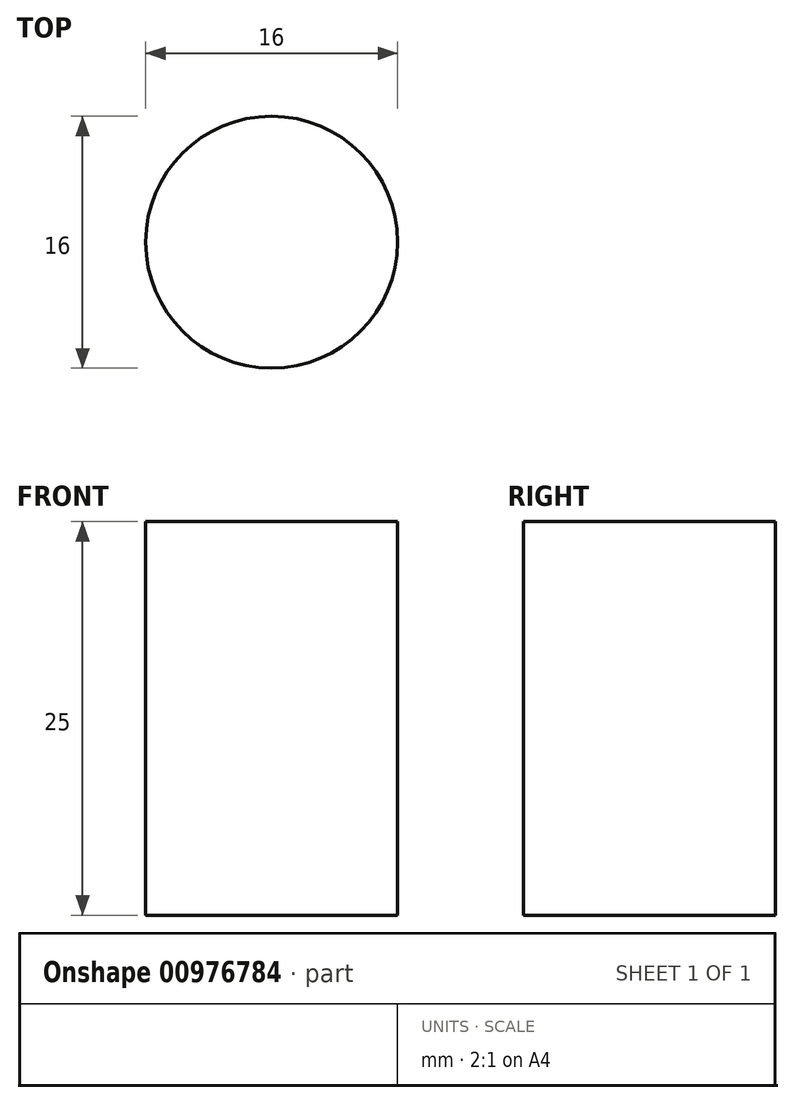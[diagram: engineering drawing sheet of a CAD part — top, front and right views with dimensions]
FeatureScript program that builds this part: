
annotation { "Feature Type Name" : "Feature", "Feature Type Description" : "" }
export const myFeature = defineFeature(function(context is Context, id is Id, definition is map)
    precondition{}
    {
        {
            var Q0;
            Q0=qCreatedBy(makeId("Top.planeOp"),FACE);
            var sketch = newSketch(context, id + "F0", { "sketchPlane" : qUnion([Q0])});
            skCircle(sketch, "E0", {"center": v(-27.11, 19.72) * mm, "radius": 8 * mm});
            skCircle(sketch, "E1", {"center": v(-10.34, 31.9) * mm, "radius": 8 * mm});
            skCircle(sketch, "E2", {"center": v(10.38, 31.88) * mm, "radius": 8 * mm});
            skCircle(sketch, "E3", {"center": v(27.13, 19.69) * mm, "radius": 8 * mm});
            skCircle(sketch, "E4", {"center": v(33.52, -0.02) * mm, "radius": 8 * mm});
            skCircle(sketch, "E5", {"center": v(27.11, -19.72) * mm, "radius": 8 * mm});
            skCircle(sketch, "E6", {"center": v(10.34, -31.9) * mm, "radius": 8 * mm});
            skCircle(sketch, "E7", {"center": v(-10.38, -31.88) * mm, "radius": 8 * mm});
            skCircle(sketch, "E8", {"center": v(-27.13, -19.69) * mm, "radius": 8 * mm});
            skCircle(sketch, "E9", {"center": v(-33.52, 0.02) * mm, "radius": 8 * mm});
            skCircle(sketch, "E10", {"center": v(0, 0) * mm, "radius": 11 * mm});
            skArc(sketch, "E11", {"start": v(4.75, 47.29) * mm, "mid": v(4.67, 47.25) * mm, "end": v(4.61, 47.18) * mm});
            skArc(sketch, "E12", {"start": v(4.61, 47.18) * mm, "mid": v(4.58, 47.11) * mm, "end": v(4.55, 47.04) * mm});
            skArc(sketch, "E13", {"start": v(3.36, 47.14) * mm, "mid": v(3.91, 46.61) * mm, "end": v(4.55, 47.04) * mm});
            skArc(sketch, "E14", {"start": v(3.36, 47.14) * mm, "mid": v(3.34, 47.22) * mm, "end": v(3.32, 47.3) * mm});
            skArc(sketch, "E15", {"start": v(3.32, 47.3) * mm, "mid": v(3.27, 47.37) * mm, "end": v(3.2, 47.42) * mm});
            skArc(sketch, "E16", {"start": v(5.18, 47.24) * mm, "mid": v(4.97, 47.26) * mm, "end": v(4.75, 47.29) * mm});
            skArc(sketch, "E17", {"start": v(6.73, 47.05) * mm, "mid": v(6.65, 47.01) * mm, "end": v(6.59, 46.95) * mm});
            skArc(sketch, "E18", {"start": v(6.59, 46.95) * mm, "mid": v(6.55, 46.88) * mm, "end": v(6.52, 46.81) * mm});
            skArc(sketch, "E19", {"start": v(5.33, 46.96) * mm, "mid": v(5.86, 46.4) * mm, "end": v(6.52, 46.81) * mm});
            skArc(sketch, "E20", {"start": v(5.33, 46.96) * mm, "mid": v(5.32, 47.04) * mm, "end": v(5.3, 47.1) * mm});
            skArc(sketch, "E21", {"start": v(5.3, 47.1) * mm, "mid": v(5.25, 47.19) * mm, "end": v(5.18, 47.24) * mm});
            skArc(sketch, "E22", {"start": v(7.16, 46.98) * mm, "mid": v(6.94, 47.02) * mm, "end": v(6.73, 47.05) * mm});
            skArc(sketch, "E23", {"start": v(8.7, 46.72) * mm, "mid": v(8.61, 46.7) * mm, "end": v(8.55, 46.63) * mm});
            skArc(sketch, "E24", {"start": v(8.55, 46.63) * mm, "mid": v(8.5, 46.57) * mm, "end": v(8.47, 46.5) * mm});
            skArc(sketch, "E25", {"start": v(7.29, 46.7) * mm, "mid": v(7.8, 46.12) * mm, "end": v(8.47, 46.5) * mm});
            skArc(sketch, "E26", {"start": v(7.29, 46.7) * mm, "mid": v(7.28, 46.77) * mm, "end": v(7.26, 46.85) * mm});
            skArc(sketch, "E27", {"start": v(7.26, 46.85) * mm, "mid": v(7.22, 46.93) * mm, "end": v(7.16, 46.98) * mm});
            skArc(sketch, "E28", {"start": v(9.12, 46.64) * mm, "mid": v(8.9, 46.68) * mm, "end": v(8.7, 46.72) * mm});
            skArc(sketch, "E29", {"start": v(10.64, 46.32) * mm, "mid": v(10.56, 46.29) * mm, "end": v(10.5, 46.23) * mm});
            skArc(sketch, "E30", {"start": v(10.5, 46.23) * mm, "mid": v(10.45, 46.17) * mm, "end": v(10.41, 46.1) * mm});
            skArc(sketch, "E31", {"start": v(9.24, 46.35) * mm, "mid": v(9.73, 45.75) * mm, "end": v(10.41, 46.1) * mm});
            skArc(sketch, "E32", {"start": v(9.24, 46.35) * mm, "mid": v(9.23, 46.43) * mm, "end": v(9.22, 46.5) * mm});
            skArc(sketch, "E33", {"start": v(9.22, 46.5) * mm, "mid": v(9.18, 46.58) * mm, "end": v(9.12, 46.64) * mm});
            skArc(sketch, "E34", {"start": v(11.06, 46.22) * mm, "mid": v(10.85, 46.27) * mm, "end": v(10.64, 46.32) * mm});
            skArc(sketch, "E35", {"start": v(12.57, 45.83) * mm, "mid": v(12.49, 45.8) * mm, "end": v(12.42, 45.75) * mm});
            skArc(sketch, "E36", {"start": v(12.42, 45.75) * mm, "mid": v(12.37, 45.7) * mm, "end": v(12.33, 45.62) * mm});
            skArc(sketch, "E37", {"start": v(11.17, 45.92) * mm, "mid": v(11.63, 45.3) * mm, "end": v(12.33, 45.62) * mm});
            skArc(sketch, "E38", {"start": v(11.17, 45.92) * mm, "mid": v(11.17, 46) * mm, "end": v(11.16, 46.07) * mm});
            skArc(sketch, "E39", {"start": v(11.16, 46.07) * mm, "mid": v(11.12, 46.16) * mm, "end": v(11.06, 46.22) * mm});
            skArc(sketch, "E40", {"start": v(12.99, 45.72) * mm, "mid": v(12.78, 45.77) * mm, "end": v(12.57, 45.83) * mm});
            skArc(sketch, "E41", {"start": v(14.48, 45.27) * mm, "mid": v(14.4, 45.24) * mm, "end": v(14.32, 45.2) * mm});
            skArc(sketch, "E42", {"start": v(14.32, 45.2) * mm, "mid": v(14.27, 45.13) * mm, "end": v(14.23, 45.07) * mm});
            skArc(sketch, "E43", {"start": v(13.08, 45.41) * mm, "mid": v(13.52, 44.78) * mm, "end": v(14.23, 45.07) * mm});
            skArc(sketch, "E44", {"start": v(13.08, 45.41) * mm, "mid": v(13.09, 45.5) * mm, "end": v(13.08, 45.57) * mm});
            skArc(sketch, "E45", {"start": v(13.08, 45.57) * mm, "mid": v(13.05, 45.65) * mm, "end": v(12.99, 45.72) * mm});
            skArc(sketch, "E46", {"start": v(14.9, 45.13) * mm, "mid": v(14.69, 45.2) * mm, "end": v(14.48, 45.27) * mm});
            skArc(sketch, "E47", {"start": v(16.36, 44.62) * mm, "mid": v(16.28, 44.6) * mm, "end": v(16.2, 44.55) * mm});
            skArc(sketch, "E48", {"start": v(16.2, 44.55) * mm, "mid": v(16.15, 44.5) * mm, "end": v(16.1, 44.43) * mm});
            skArc(sketch, "E49", {"start": v(14.97, 44.83) * mm, "mid": v(15.38, 44.17) * mm, "end": v(16.1, 44.43) * mm});
            skArc(sketch, "E50", {"start": v(14.97, 44.83) * mm, "mid": v(14.98, 44.9) * mm, "end": v(14.97, 44.98) * mm});
            skArc(sketch, "E51", {"start": v(14.97, 44.98) * mm, "mid": v(14.95, 45.06) * mm, "end": v(14.9, 45.13) * mm});
            skArc(sketch, "E52", {"start": v(16.77, 44.47) * mm, "mid": v(16.57, 44.54) * mm, "end": v(16.36, 44.62) * mm});
            skArc(sketch, "E53", {"start": v(18.22, 43.9) * mm, "mid": v(18.13, 43.88) * mm, "end": v(18.05, 43.83) * mm});
            skArc(sketch, "E54", {"start": v(18.05, 43.83) * mm, "mid": v(18, 43.78) * mm, "end": v(17.96, 43.72) * mm});
            skArc(sketch, "E55", {"start": v(16.84, 44.16) * mm, "mid": v(17.22, 43.5) * mm, "end": v(17.96, 43.72) * mm});
            skArc(sketch, "E56", {"start": v(16.84, 44.16) * mm, "mid": v(16.85, 44.24) * mm, "end": v(16.85, 44.31) * mm});
            skArc(sketch, "E57", {"start": v(16.85, 44.31) * mm, "mid": v(16.82, 44.4) * mm, "end": v(16.77, 44.47) * mm});
            skArc(sketch, "E58", {"start": v(18.62, 43.73) * mm, "mid": v(18.42, 43.81) * mm, "end": v(18.22, 43.9) * mm});
            skArc(sketch, "E59", {"start": v(20.04, 43.1) * mm, "mid": v(19.95, 43.08) * mm, "end": v(19.87, 43.04) * mm});
            skArc(sketch, "E60", {"start": v(19.87, 43.04) * mm, "mid": v(19.82, 42.99) * mm, "end": v(19.77, 42.93) * mm});
            skArc(sketch, "E61", {"start": v(18.67, 43.42) * mm, "mid": v(19.03, 42.73) * mm, "end": v(19.77, 42.93) * mm});
            skArc(sketch, "E62", {"start": v(18.67, 43.42) * mm, "mid": v(18.68, 43.5) * mm, "end": v(18.69, 43.57) * mm});
            skArc(sketch, "E63", {"start": v(18.69, 43.57) * mm, "mid": v(18.67, 43.65) * mm, "end": v(18.62, 43.73) * mm});
            skArc(sketch, "E64", {"start": v(20.43, 42.9) * mm, "mid": v(20.24, 43) * mm, "end": v(20.04, 43.1) * mm});
            skArc(sketch, "E65", {"start": v(21.83, 42.22) * mm, "mid": v(21.74, 42.2) * mm, "end": v(21.66, 42.17) * mm});
            skArc(sketch, "E66", {"start": v(21.66, 42.17) * mm, "mid": v(21.6, 42.12) * mm, "end": v(21.55, 42.06) * mm});
            skArc(sketch, "E67", {"start": v(20.47, 42.6) * mm, "mid": v(20.8, 41.9) * mm, "end": v(21.55, 42.06) * mm});
            skArc(sketch, "E68", {"start": v(20.47, 42.6) * mm, "mid": v(20.49, 42.67) * mm, "end": v(20.5, 42.75) * mm});
            skArc(sketch, "E69", {"start": v(20.5, 42.75) * mm, "mid": v(20.48, 42.83) * mm, "end": v(20.43, 42.9) * mm});
            skArc(sketch, "E70", {"start": v(22.2, 42.02) * mm, "mid": v(22.02, 42.12) * mm, "end": v(21.83, 42.22) * mm});
            skArc(sketch, "E71", {"start": v(23.58, 41.27) * mm, "mid": v(23.49, 41.26) * mm, "end": v(23.4, 41.23) * mm});
            skArc(sketch, "E72", {"start": v(23.4, 41.23) * mm, "mid": v(23.35, 41.18) * mm, "end": v(23.3, 41.12) * mm});
            skArc(sketch, "E73", {"start": v(22.24, 41.7) * mm, "mid": v(22.53, 40.99) * mm, "end": v(23.3, 41.12) * mm});
            skArc(sketch, "E74", {"start": v(22.24, 41.7) * mm, "mid": v(22.26, 41.78) * mm, "end": v(22.27, 41.85) * mm});
            skArc(sketch, "E75", {"start": v(22.27, 41.85) * mm, "mid": v(22.25, 41.94) * mm, "end": v(22.2, 42.02) * mm});
            skArc(sketch, "E76", {"start": v(23.95, 41.05) * mm, "mid": v(23.76, 41.16) * mm, "end": v(23.58, 41.27) * mm});
            skArc(sketch, "E77", {"start": v(25.28, 40.24) * mm, "mid": v(25.2, 40.24) * mm, "end": v(25.11, 40.2) * mm});
            skArc(sketch, "E78", {"start": v(25.11, 40.2) * mm, "mid": v(25.05, 40.16) * mm, "end": v(25, 40.11) * mm});
            skArc(sketch, "E79", {"start": v(23.97, 40.73) * mm, "mid": v(24.23, 40.01) * mm, "end": v(25, 40.11) * mm});
            skArc(sketch, "E80", {"start": v(23.97, 40.73) * mm, "mid": v(23.99, 40.8) * mm, "end": v(24, 40.88) * mm});
            skArc(sketch, "E81", {"start": v(24, 40.88) * mm, "mid": v(24, 40.97) * mm, "end": v(23.95, 41.05) * mm});
            skArc(sketch, "E82", {"start": v(25.65, 40.01) * mm, "mid": v(25.47, 40.13) * mm, "end": v(25.28, 40.24) * mm});
            skArc(sketch, "E83", {"start": v(26.95, 39.15) * mm, "mid": v(26.86, 39.15) * mm, "end": v(26.77, 39.12) * mm});
            skArc(sketch, "E84", {"start": v(26.77, 39.12) * mm, "mid": v(26.71, 39.08) * mm, "end": v(26.65, 39.03) * mm});
            skArc(sketch, "E85", {"start": v(25.65, 39.7) * mm, "mid": v(25.89, 38.96) * mm, "end": v(26.65, 39.03) * mm});
            skArc(sketch, "E86", {"start": v(25.65, 39.7) * mm, "mid": v(25.68, 39.77) * mm, "end": v(25.7, 39.84) * mm});
            skArc(sketch, "E87", {"start": v(25.7, 39.84) * mm, "mid": v(25.69, 39.93) * mm, "end": v(25.65, 40.01) * mm});
            skArc(sketch, "E88", {"start": v(27.3, 38.9) * mm, "mid": v(27.12, 39.03) * mm, "end": v(26.95, 39.15) * mm});
            skArc(sketch, "E89", {"start": v(28.56, 37.99) * mm, "mid": v(28.47, 38) * mm, "end": v(28.39, 37.97) * mm});
            skArc(sketch, "E90", {"start": v(28.39, 37.97) * mm, "mid": v(28.32, 37.93) * mm, "end": v(28.26, 37.88) * mm});
            skArc(sketch, "E91", {"start": v(27.3, 38.59) * mm, "mid": v(27.5, 37.84) * mm, "end": v(28.26, 37.88) * mm});
            skArc(sketch, "E92", {"start": v(27.3, 38.59) * mm, "mid": v(27.32, 38.66) * mm, "end": v(27.34, 38.73) * mm});
            skArc(sketch, "E93", {"start": v(27.34, 38.73) * mm, "mid": v(27.33, 38.82) * mm, "end": v(27.3, 38.9) * mm});
            skArc(sketch, "E94", {"start": v(28.9, 37.72) * mm, "mid": v(28.73, 37.86) * mm, "end": v(28.56, 37.99) * mm});
            skArc(sketch, "E95", {"start": v(30.13, 36.76) * mm, "mid": v(30.04, 36.77) * mm, "end": v(29.95, 36.74) * mm});
            skArc(sketch, "E96", {"start": v(29.95, 36.74) * mm, "mid": v(29.89, 36.7) * mm, "end": v(29.82, 36.66) * mm});
            skArc(sketch, "E97", {"start": v(28.88, 37.4) * mm, "mid": v(29.05, 36.66) * mm, "end": v(29.82, 36.66) * mm});
            skArc(sketch, "E98", {"start": v(28.88, 37.4) * mm, "mid": v(28.91, 37.48) * mm, "end": v(28.93, 37.55) * mm});
            skArc(sketch, "E99", {"start": v(28.93, 37.55) * mm, "mid": v(28.94, 37.64) * mm, "end": v(28.9, 37.72) * mm});
            skArc(sketch, "E100", {"start": v(30.46, 36.48) * mm, "mid": v(30.3, 36.62) * mm, "end": v(30.13, 36.76) * mm});
            skArc(sketch, "E101", {"start": v(31.64, 35.46) * mm, "mid": v(31.55, 35.48) * mm, "end": v(31.47, 35.46) * mm});
            skArc(sketch, "E102", {"start": v(31.47, 35.46) * mm, "mid": v(31.4, 35.42) * mm, "end": v(31.33, 35.38) * mm});
            skArc(sketch, "E103", {"start": v(30.43, 36.17) * mm, "mid": v(30.56, 35.4) * mm, "end": v(31.33, 35.38) * mm});
            skArc(sketch, "E104", {"start": v(30.43, 36.17) * mm, "mid": v(30.46, 36.24) * mm, "end": v(30.48, 36.3) * mm});
            skArc(sketch, "E105", {"start": v(30.48, 36.3) * mm, "mid": v(30.49, 36.4) * mm, "end": v(30.46, 36.48) * mm});
            skArc(sketch, "E106", {"start": v(31.96, 35.17) * mm, "mid": v(31.8, 35.32) * mm, "end": v(31.64, 35.46) * mm});
            skArc(sketch, "E107", {"start": v(33.1, 34.1) * mm, "mid": v(33.01, 34.12) * mm, "end": v(32.92, 34.1) * mm});
            skArc(sketch, "E108", {"start": v(32.92, 34.1) * mm, "mid": v(32.85, 34.08) * mm, "end": v(32.79, 34.04) * mm});
            skArc(sketch, "E109", {"start": v(31.91, 34.86) * mm, "mid": v(32.02, 34.1) * mm, "end": v(32.79, 34.04) * mm});
            skArc(sketch, "E110", {"start": v(31.91, 34.86) * mm, "mid": v(31.95, 34.93) * mm, "end": v(31.98, 35) * mm});
            skArc(sketch, "E111", {"start": v(31.98, 35) * mm, "mid": v(31.98, 35.09) * mm, "end": v(31.96, 35.17) * mm});
            skArc(sketch, "E112", {"start": v(33.4, 33.8) * mm, "mid": v(33.25, 33.96) * mm, "end": v(33.1, 34.1) * mm});
            skArc(sketch, "E113", {"start": v(34.5, 32.7) * mm, "mid": v(34.41, 32.71) * mm, "end": v(34.32, 32.7) * mm});
            skArc(sketch, "E114", {"start": v(34.32, 32.7) * mm, "mid": v(34.25, 32.67) * mm, "end": v(34.18, 32.64) * mm});
            skArc(sketch, "E115", {"start": v(33.34, 33.5) * mm, "mid": v(33.42, 32.73) * mm, "end": v(34.18, 32.64) * mm});
            skArc(sketch, "E116", {"start": v(33.34, 33.5) * mm, "mid": v(33.38, 33.56) * mm, "end": v(33.41, 33.63) * mm});
            skArc(sketch, "E117", {"start": v(33.41, 33.63) * mm, "mid": v(33.43, 33.72) * mm, "end": v(33.4, 33.8) * mm});
            skArc(sketch, "E118", {"start": v(34.8, 32.38) * mm, "mid": v(34.64, 32.53) * mm, "end": v(34.5, 32.7) * mm});
            skArc(sketch, "E119", {"start": v(35.83, 31.22) * mm, "mid": v(35.75, 31.24) * mm, "end": v(35.66, 31.24) * mm});
            skArc(sketch, "E120", {"start": v(35.66, 31.24) * mm, "mid": v(35.59, 31.2) * mm, "end": v(35.52, 31.18) * mm});
            skArc(sketch, "E121", {"start": v(34.72, 32.07) * mm, "mid": v(34.76, 31.3) * mm, "end": v(35.52, 31.18) * mm});
            skArc(sketch, "E122", {"start": v(34.72, 32.07) * mm, "mid": v(34.76, 32.13) * mm, "end": v(34.8, 32.2) * mm});
            skArc(sketch, "E123", {"start": v(34.8, 32.2) * mm, "mid": v(34.8, 32.29) * mm, "end": v(34.8, 32.38) * mm});
            skArc(sketch, "E124", {"start": v(36.12, 30.89) * mm, "mid": v(35.98, 31.05) * mm, "end": v(35.83, 31.22) * mm});
            skArc(sketch, "E125", {"start": v(37.11, 29.69) * mm, "mid": v(37.03, 29.72) * mm, "end": v(36.94, 29.71) * mm});
            skArc(sketch, "E126", {"start": v(36.94, 29.71) * mm, "mid": v(36.87, 29.7) * mm, "end": v(36.8, 29.66) * mm});
            skArc(sketch, "E127", {"start": v(36.03, 30.59) * mm, "mid": v(36.04, 29.82) * mm, "end": v(36.8, 29.66) * mm});
            skArc(sketch, "E128", {"start": v(36.03, 30.59) * mm, "mid": v(36.07, 30.65) * mm, "end": v(36.1, 30.72) * mm});
            skArc(sketch, "E129", {"start": v(36.1, 30.72) * mm, "mid": v(36.13, 30.8) * mm, "end": v(36.12, 30.89) * mm});
            skArc(sketch, "E130", {"start": v(37.38, 29.35) * mm, "mid": v(37.25, 29.52) * mm, "end": v(37.11, 29.69) * mm});
            skArc(sketch, "E131", {"start": v(38.32, 28.1) * mm, "mid": v(38.24, 28.14) * mm, "end": v(38.15, 28.14) * mm});
            skArc(sketch, "E132", {"start": v(38.15, 28.14) * mm, "mid": v(38.08, 28.12) * mm, "end": v(38, 28.1) * mm});
            skArc(sketch, "E133", {"start": v(37.28, 29.05) * mm, "mid": v(37.26, 28.28) * mm, "end": v(38, 28.1) * mm});
            skArc(sketch, "E134", {"start": v(37.28, 29.05) * mm, "mid": v(37.33, 29.11) * mm, "end": v(37.36, 29.18) * mm});
            skArc(sketch, "E135", {"start": v(37.36, 29.18) * mm, "mid": v(37.39, 29.26) * mm, "end": v(37.38, 29.35) * mm});
            skArc(sketch, "E136", {"start": v(38.58, 27.76) * mm, "mid": v(38.45, 27.93) * mm, "end": v(38.32, 28.1) * mm});
            skArc(sketch, "E137", {"start": v(39.46, 26.48) * mm, "mid": v(39.38, 26.52) * mm, "end": v(39.3, 26.52) * mm});
            skArc(sketch, "E138", {"start": v(39.3, 26.52) * mm, "mid": v(39.22, 26.5) * mm, "end": v(39.15, 26.48) * mm});
            skArc(sketch, "E139", {"start": v(38.46, 27.46) * mm, "mid": v(38.4, 26.7) * mm, "end": v(39.15, 26.48) * mm});
            skArc(sketch, "E140", {"start": v(38.46, 27.46) * mm, "mid": v(38.51, 27.52) * mm, "end": v(38.55, 27.59) * mm});
            skArc(sketch, "E141", {"start": v(38.55, 27.59) * mm, "mid": v(38.58, 27.67) * mm, "end": v(38.58, 27.76) * mm});
            skArc(sketch, "E142", {"start": v(39.7, 26.12) * mm, "mid": v(39.58, 26.3) * mm, "end": v(39.46, 26.48) * mm});
            skArc(sketch, "E143", {"start": v(40.54, 24.8) * mm, "mid": v(40.46, 24.84) * mm, "end": v(40.37, 24.85) * mm});
            skArc(sketch, "E144", {"start": v(40.37, 24.85) * mm, "mid": v(40.3, 24.84) * mm, "end": v(40.22, 24.82) * mm});
            skArc(sketch, "E145", {"start": v(39.58, 25.83) * mm, "mid": v(39.5, 25.06) * mm, "end": v(40.22, 24.82) * mm});
            skArc(sketch, "E146", {"start": v(39.58, 25.83) * mm, "mid": v(39.63, 25.89) * mm, "end": v(39.67, 25.95) * mm});
            skArc(sketch, "E147", {"start": v(39.67, 25.95) * mm, "mid": v(39.7, 26.03) * mm, "end": v(39.7, 26.12) * mm});
            skArc(sketch, "E148", {"start": v(40.76, 24.43) * mm, "mid": v(40.65, 24.62) * mm, "end": v(40.54, 24.8) * mm});
            skArc(sketch, "E149", {"start": v(41.54, 23.08) * mm, "mid": v(41.46, 23.13) * mm, "end": v(41.38, 23.14) * mm});
            skArc(sketch, "E150", {"start": v(41.38, 23.14) * mm, "mid": v(41.3, 23.13) * mm, "end": v(41.23, 23.1) * mm});
            skArc(sketch, "E151", {"start": v(40.63, 24.15) * mm, "mid": v(40.5, 23.39) * mm, "end": v(41.23, 23.1) * mm});
            skArc(sketch, "E152", {"start": v(40.63, 24.15) * mm, "mid": v(40.68, 24.2) * mm, "end": v(40.73, 24.26) * mm});
            skArc(sketch, "E153", {"start": v(40.73, 24.26) * mm, "mid": v(40.76, 24.35) * mm, "end": v(40.76, 24.43) * mm});
            skArc(sketch, "E154", {"start": v(41.75, 22.7) * mm, "mid": v(41.65, 22.9) * mm, "end": v(41.54, 23.08) * mm});
            skArc(sketch, "E155", {"start": v(42.47, 21.32) * mm, "mid": v(42.4, 21.37) * mm, "end": v(42.3, 21.38) * mm});
            skArc(sketch, "E156", {"start": v(42.3, 21.38) * mm, "mid": v(42.23, 21.38) * mm, "end": v(42.16, 21.36) * mm});
            skArc(sketch, "E157", {"start": v(41.6, 22.43) * mm, "mid": v(41.45, 21.67) * mm, "end": v(42.16, 21.36) * mm});
            skArc(sketch, "E158", {"start": v(41.6, 22.43) * mm, "mid": v(41.66, 22.48) * mm, "end": v(41.7, 22.54) * mm});
            skArc(sketch, "E159", {"start": v(41.7, 22.54) * mm, "mid": v(41.74, 22.62) * mm, "end": v(41.75, 22.7) * mm});
            skArc(sketch, "E160", {"start": v(42.66, 20.94) * mm, "mid": v(42.57, 21.13) * mm, "end": v(42.47, 21.32) * mm});
            skArc(sketch, "E161", {"start": v(43.33, 19.53) * mm, "mid": v(43.25, 19.58) * mm, "end": v(43.17, 19.6) * mm});
            skArc(sketch, "E162", {"start": v(43.17, 19.6) * mm, "mid": v(43.1, 19.6) * mm, "end": v(43.02, 19.58) * mm});
            skArc(sketch, "E163", {"start": v(42.5, 20.66) * mm, "mid": v(42.32, 19.92) * mm, "end": v(43.02, 19.58) * mm});
            skArc(sketch, "E164", {"start": v(42.5, 20.66) * mm, "mid": v(42.56, 20.71) * mm, "end": v(42.61, 20.77) * mm});
            skArc(sketch, "E165", {"start": v(42.61, 20.77) * mm, "mid": v(42.66, 20.85) * mm, "end": v(42.66, 20.94) * mm});
            skArc(sketch, "E166", {"start": v(43.5, 19.13) * mm, "mid": v(43.42, 19.33) * mm, "end": v(43.33, 19.53) * mm});
            skArc(sketch, "E167", {"start": v(44.1, 17.7) * mm, "mid": v(44.04, 17.75) * mm, "end": v(43.95, 17.77) * mm});
            skArc(sketch, "E168", {"start": v(43.95, 17.77) * mm, "mid": v(43.87, 17.77) * mm, "end": v(43.8, 17.76) * mm});
            skArc(sketch, "E169", {"start": v(43.33, 18.87) * mm, "mid": v(43.12, 18.13) * mm, "end": v(43.8, 17.76) * mm});
            skArc(sketch, "E170", {"start": v(43.33, 18.87) * mm, "mid": v(43.4, 18.91) * mm, "end": v(43.45, 18.97) * mm});
            skArc(sketch, "E171", {"start": v(43.45, 18.97) * mm, "mid": v(43.5, 19.04) * mm, "end": v(43.5, 19.13) * mm});
            skArc(sketch, "E172", {"start": v(44.27, 17.3) * mm, "mid": v(44.19, 17.5) * mm, "end": v(44.1, 17.7) * mm});
            skArc(sketch, "E173", {"start": v(44.8, 15.83) * mm, "mid": v(44.74, 15.89) * mm, "end": v(44.66, 15.91) * mm});
            skArc(sketch, "E174", {"start": v(44.66, 15.91) * mm, "mid": v(44.58, 15.92) * mm, "end": v(44.5, 15.91) * mm});
            skArc(sketch, "E175", {"start": v(44.09, 17.04) * mm, "mid": v(43.84, 16.3) * mm, "end": v(44.5, 15.91) * mm});
            skArc(sketch, "E176", {"start": v(44.09, 17.04) * mm, "mid": v(44.15, 17.08) * mm, "end": v(44.2, 17.13) * mm});
            skArc(sketch, "E177", {"start": v(44.2, 17.13) * mm, "mid": v(44.25, 17.2) * mm, "end": v(44.27, 17.3) * mm});
            skArc(sketch, "E178", {"start": v(44.95, 15.43) * mm, "mid": v(44.88, 15.63) * mm, "end": v(44.8, 15.83) * mm});
            skArc(sketch, "E179", {"start": v(45.43, 13.94) * mm, "mid": v(45.37, 14) * mm, "end": v(45.28, 14.03) * mm});
            skArc(sketch, "E180", {"start": v(45.28, 14.03) * mm, "mid": v(45.2, 14.04) * mm, "end": v(45.13, 14.03) * mm});
            skArc(sketch, "E181", {"start": v(44.76, 15.17) * mm, "mid": v(44.49, 14.45) * mm, "end": v(45.13, 14.03) * mm});
            skArc(sketch, "E182", {"start": v(44.76, 15.17) * mm, "mid": v(44.82, 15.22) * mm, "end": v(44.88, 15.27) * mm});
            skArc(sketch, "E183", {"start": v(44.88, 15.27) * mm, "mid": v(44.93, 15.34) * mm, "end": v(44.95, 15.43) * mm});
            skArc(sketch, "E184", {"start": v(45.56, 13.53) * mm, "mid": v(45.5, 13.74) * mm, "end": v(45.43, 13.94) * mm});
            skArc(sketch, "E185", {"start": v(45.98, 12.03) * mm, "mid": v(45.91, 12.09) * mm, "end": v(45.83, 12.12) * mm});
            skArc(sketch, "E186", {"start": v(45.83, 12.12) * mm, "mid": v(45.76, 12.13) * mm, "end": v(45.68, 12.13) * mm});
            skArc(sketch, "E187", {"start": v(45.36, 13.29) * mm, "mid": v(45.05, 12.58) * mm, "end": v(45.68, 12.13) * mm});
            skArc(sketch, "E188", {"start": v(45.36, 13.29) * mm, "mid": v(45.42, 13.33) * mm, "end": v(45.48, 13.37) * mm});
            skArc(sketch, "E189", {"start": v(45.48, 13.37) * mm, "mid": v(45.54, 13.44) * mm, "end": v(45.56, 13.53) * mm});
            skArc(sketch, "E190", {"start": v(46.09, 11.6) * mm, "mid": v(46.03, 11.82) * mm, "end": v(45.98, 12.03) * mm});
            skArc(sketch, "E191", {"start": v(46.44, 10.1) * mm, "mid": v(46.38, 10.16) * mm, "end": v(46.3, 10.2) * mm});
            skArc(sketch, "E192", {"start": v(46.3, 10.2) * mm, "mid": v(46.22, 10.2) * mm, "end": v(46.15, 10.2) * mm});
            skArc(sketch, "E193", {"start": v(45.87, 11.38) * mm, "mid": v(45.54, 10.68) * mm, "end": v(46.15, 10.2) * mm});
            skArc(sketch, "E194", {"start": v(45.87, 11.38) * mm, "mid": v(45.94, 11.41) * mm, "end": v(46, 11.46) * mm});
            skArc(sketch, "E195", {"start": v(46, 11.46) * mm, "mid": v(46.06, 11.53) * mm, "end": v(46.09, 11.6) * mm});
            skArc(sketch, "E196", {"start": v(46.53, 9.67) * mm, "mid": v(46.49, 9.88) * mm, "end": v(46.44, 10.1) * mm});
            skArc(sketch, "E197", {"start": v(46.82, 8.14) * mm, "mid": v(46.76, 8.2) * mm, "end": v(46.68, 8.24) * mm});
            skArc(sketch, "E198", {"start": v(46.68, 8.24) * mm, "mid": v(46.6, 8.26) * mm, "end": v(46.53, 8.27) * mm});
            skArc(sketch, "E199", {"start": v(46.3, 9.45) * mm, "mid": v(45.95, 8.76) * mm, "end": v(46.53, 8.27) * mm});
            skArc(sketch, "E200", {"start": v(46.3, 9.45) * mm, "mid": v(46.38, 9.48) * mm, "end": v(46.44, 9.52) * mm});
            skArc(sketch, "E201", {"start": v(46.44, 9.52) * mm, "mid": v(46.5, 9.59) * mm, "end": v(46.53, 9.67) * mm});
            skArc(sketch, "E202", {"start": v(46.9, 7.71) * mm, "mid": v(46.86, 7.93) * mm, "end": v(46.82, 8.14) * mm});
            skArc(sketch, "E203", {"start": v(47.12, 6.17) * mm, "mid": v(47.07, 6.24) * mm, "end": v(46.99, 6.28) * mm});
            skArc(sketch, "E204", {"start": v(46.99, 6.28) * mm, "mid": v(46.91, 6.3) * mm, "end": v(46.84, 6.3) * mm});
            skArc(sketch, "E205", {"start": v(46.66, 7.5) * mm, "mid": v(46.27, 6.83) * mm, "end": v(46.84, 6.3) * mm});
            skArc(sketch, "E206", {"start": v(46.66, 7.5) * mm, "mid": v(46.73, 7.53) * mm, "end": v(46.8, 7.57) * mm});
            skArc(sketch, "E207", {"start": v(46.8, 7.57) * mm, "mid": v(46.86, 7.63) * mm, "end": v(46.9, 7.71) * mm});
            skArc(sketch, "E208", {"start": v(47.18, 5.74) * mm, "mid": v(47.15, 5.96) * mm, "end": v(47.12, 6.17) * mm});
            skArc(sketch, "E209", {"start": v(47.34, 4.2) * mm, "mid": v(47.29, 4.26) * mm, "end": v(47.21, 4.3) * mm});
            skArc(sketch, "E210", {"start": v(47.21, 4.3) * mm, "mid": v(47.14, 4.33) * mm, "end": v(47.06, 4.34) * mm});
            skArc(sketch, "E211", {"start": v(46.94, 5.54) * mm, "mid": v(46.52, 4.89) * mm, "end": v(47.06, 4.34) * mm});
            skArc(sketch, "E212", {"start": v(46.94, 5.54) * mm, "mid": v(47, 5.57) * mm, "end": v(47.07, 5.6) * mm});
            skArc(sketch, "E213", {"start": v(47.07, 5.6) * mm, "mid": v(47.14, 5.66) * mm, "end": v(47.18, 5.74) * mm});
            skArc(sketch, "E214", {"start": v(47.38, 3.76) * mm, "mid": v(47.36, 3.98) * mm, "end": v(47.34, 4.2) * mm});
            skArc(sketch, "E215", {"start": v(47.47, 2.2) * mm, "mid": v(47.42, 2.28) * mm, "end": v(47.35, 2.33) * mm});
            skArc(sketch, "E216", {"start": v(47.35, 2.33) * mm, "mid": v(47.28, 2.35) * mm, "end": v(47.2, 2.37) * mm});
            skArc(sketch, "E217", {"start": v(47.13, 3.57) * mm, "mid": v(46.68, 2.94) * mm, "end": v(47.2, 2.37) * mm});
            skArc(sketch, "E218", {"start": v(47.13, 3.57) * mm, "mid": v(47.2, 3.6) * mm, "end": v(47.27, 3.63) * mm});
            skArc(sketch, "E219", {"start": v(47.27, 3.63) * mm, "mid": v(47.34, 3.68) * mm, "end": v(47.38, 3.76) * mm});
            skArc(sketch, "E220", {"start": v(47.5, 1.77) * mm, "mid": v(47.48, 2) * mm, "end": v(47.47, 2.2) * mm});
            skArc(sketch, "E221", {"start": v(47.52, 0.22) * mm, "mid": v(47.48, 0.3) * mm, "end": v(47.4, 0.34) * mm});
            skArc(sketch, "E222", {"start": v(47.4, 0.34) * mm, "mid": v(47.33, 0.37) * mm, "end": v(47.26, 0.39) * mm});
            skArc(sketch, "E223", {"start": v(47.24, 1.59) * mm, "mid": v(46.77, 0.98) * mm, "end": v(47.26, 0.39) * mm});
            skArc(sketch, "E224", {"start": v(47.24, 1.59) * mm, "mid": v(47.3, 1.61) * mm, "end": v(47.38, 1.64) * mm});
            skArc(sketch, "E225", {"start": v(47.38, 1.64) * mm, "mid": v(47.45, 1.7) * mm, "end": v(47.5, 1.77) * mm});
            skArc(sketch, "E226", {"start": v(47.52, -0.22) * mm, "mid": v(47.52, 0) * mm, "end": v(47.52, 0.22) * mm});
            skArc(sketch, "E227", {"start": v(47.5, -1.77) * mm, "mid": v(47.45, -1.7) * mm, "end": v(47.38, -1.64) * mm});
            skArc(sketch, "E228", {"start": v(47.38, -1.64) * mm, "mid": v(47.3, -1.61) * mm, "end": v(47.24, -1.59) * mm});
            skArc(sketch, "E229", {"start": v(47.26, -0.39) * mm, "mid": v(46.77, -0.98) * mm, "end": v(47.24, -1.59) * mm});
            skArc(sketch, "E230", {"start": v(47.26, -0.39) * mm, "mid": v(47.33, -0.37) * mm, "end": v(47.4, -0.34) * mm});
            skArc(sketch, "E231", {"start": v(47.4, -0.34) * mm, "mid": v(47.48, -0.3) * mm, "end": v(47.52, -0.22) * mm});
            skArc(sketch, "E232", {"start": v(47.47, -2.2) * mm, "mid": v(47.48, -2) * mm, "end": v(47.5, -1.77) * mm});
            skArc(sketch, "E233", {"start": v(47.38, -3.76) * mm, "mid": v(47.34, -3.68) * mm, "end": v(47.27, -3.63) * mm});
            skArc(sketch, "E234", {"start": v(47.27, -3.63) * mm, "mid": v(47.2, -3.6) * mm, "end": v(47.13, -3.57) * mm});
            skArc(sketch, "E235", {"start": v(47.2, -2.37) * mm, "mid": v(46.68, -2.94) * mm, "end": v(47.13, -3.57) * mm});
            skArc(sketch, "E236", {"start": v(47.2, -2.37) * mm, "mid": v(47.28, -2.35) * mm, "end": v(47.35, -2.33) * mm});
            skArc(sketch, "E237", {"start": v(47.35, -2.33) * mm, "mid": v(47.42, -2.28) * mm, "end": v(47.47, -2.2) * mm});
            skArc(sketch, "E238", {"start": v(47.34, -4.2) * mm, "mid": v(47.36, -3.98) * mm, "end": v(47.38, -3.76) * mm});
            skArc(sketch, "E239", {"start": v(47.18, -5.74) * mm, "mid": v(47.14, -5.66) * mm, "end": v(47.07, -5.6) * mm});
            skArc(sketch, "E240", {"start": v(47.07, -5.6) * mm, "mid": v(47, -5.57) * mm, "end": v(46.94, -5.54) * mm});
            skArc(sketch, "E241", {"start": v(47.06, -4.34) * mm, "mid": v(46.52, -4.89) * mm, "end": v(46.94, -5.54) * mm});
            skArc(sketch, "E242", {"start": v(47.06, -4.34) * mm, "mid": v(47.14, -4.33) * mm, "end": v(47.21, -4.3) * mm});
            skArc(sketch, "E243", {"start": v(47.21, -4.3) * mm, "mid": v(47.29, -4.26) * mm, "end": v(47.34, -4.2) * mm});
            skArc(sketch, "E244", {"start": v(47.12, -6.17) * mm, "mid": v(47.15, -5.96) * mm, "end": v(47.18, -5.74) * mm});
            skArc(sketch, "E245", {"start": v(46.9, -7.71) * mm, "mid": v(46.86, -7.63) * mm, "end": v(46.8, -7.57) * mm});
            skArc(sketch, "E246", {"start": v(46.8, -7.57) * mm, "mid": v(46.73, -7.53) * mm, "end": v(46.66, -7.5) * mm});
            skArc(sketch, "E247", {"start": v(46.84, -6.3) * mm, "mid": v(46.27, -6.83) * mm, "end": v(46.66, -7.5) * mm});
            skArc(sketch, "E248", {"start": v(46.84, -6.3) * mm, "mid": v(46.91, -6.3) * mm, "end": v(46.99, -6.28) * mm});
            skArc(sketch, "E249", {"start": v(46.99, -6.28) * mm, "mid": v(47.07, -6.24) * mm, "end": v(47.12, -6.17) * mm});
            skArc(sketch, "E250", {"start": v(46.82, -8.14) * mm, "mid": v(46.86, -7.93) * mm, "end": v(46.9, -7.71) * mm});
            skArc(sketch, "E251", {"start": v(46.53, -9.67) * mm, "mid": v(46.5, -9.59) * mm, "end": v(46.44, -9.52) * mm});
            skArc(sketch, "E252", {"start": v(46.44, -9.52) * mm, "mid": v(46.38, -9.48) * mm, "end": v(46.3, -9.45) * mm});
            skArc(sketch, "E253", {"start": v(46.53, -8.27) * mm, "mid": v(45.95, -8.76) * mm, "end": v(46.3, -9.45) * mm});
            skArc(sketch, "E254", {"start": v(46.53, -8.27) * mm, "mid": v(46.6, -8.26) * mm, "end": v(46.68, -8.24) * mm});
            skArc(sketch, "E255", {"start": v(46.68, -8.24) * mm, "mid": v(46.76, -8.2) * mm, "end": v(46.82, -8.14) * mm});
            skArc(sketch, "E256", {"start": v(46.44, -10.1) * mm, "mid": v(46.49, -9.88) * mm, "end": v(46.53, -9.67) * mm});
            skArc(sketch, "E257", {"start": v(46.09, -11.6) * mm, "mid": v(46.06, -11.53) * mm, "end": v(46, -11.46) * mm});
            skArc(sketch, "E258", {"start": v(46, -11.46) * mm, "mid": v(45.94, -11.41) * mm, "end": v(45.87, -11.38) * mm});
            skArc(sketch, "E259", {"start": v(46.15, -10.2) * mm, "mid": v(45.54, -10.68) * mm, "end": v(45.87, -11.38) * mm});
            skArc(sketch, "E260", {"start": v(46.15, -10.2) * mm, "mid": v(46.22, -10.2) * mm, "end": v(46.3, -10.2) * mm});
            skArc(sketch, "E261", {"start": v(46.3, -10.2) * mm, "mid": v(46.38, -10.16) * mm, "end": v(46.44, -10.1) * mm});
            skArc(sketch, "E262", {"start": v(45.98, -12.03) * mm, "mid": v(46.03, -11.82) * mm, "end": v(46.09, -11.6) * mm});
            skArc(sketch, "E263", {"start": v(45.56, -13.53) * mm, "mid": v(45.54, -13.44) * mm, "end": v(45.48, -13.37) * mm});
            skArc(sketch, "E264", {"start": v(45.48, -13.37) * mm, "mid": v(45.42, -13.33) * mm, "end": v(45.36, -13.29) * mm});
            skArc(sketch, "E265", {"start": v(45.68, -12.13) * mm, "mid": v(45.05, -12.58) * mm, "end": v(45.36, -13.29) * mm});
            skArc(sketch, "E266", {"start": v(45.68, -12.13) * mm, "mid": v(45.76, -12.13) * mm, "end": v(45.83, -12.12) * mm});
            skArc(sketch, "E267", {"start": v(45.83, -12.12) * mm, "mid": v(45.91, -12.09) * mm, "end": v(45.98, -12.03) * mm});
            skArc(sketch, "E268", {"start": v(45.43, -13.94) * mm, "mid": v(45.5, -13.74) * mm, "end": v(45.56, -13.53) * mm});
            skArc(sketch, "E269", {"start": v(44.95, -15.43) * mm, "mid": v(44.93, -15.34) * mm, "end": v(44.88, -15.27) * mm});
            skArc(sketch, "E270", {"start": v(44.88, -15.27) * mm, "mid": v(44.82, -15.22) * mm, "end": v(44.76, -15.17) * mm});
            skArc(sketch, "E271", {"start": v(45.13, -14.03) * mm, "mid": v(44.49, -14.45) * mm, "end": v(44.76, -15.17) * mm});
            skArc(sketch, "E272", {"start": v(45.13, -14.03) * mm, "mid": v(45.2, -14.04) * mm, "end": v(45.28, -14.03) * mm});
            skArc(sketch, "E273", {"start": v(45.28, -14.03) * mm, "mid": v(45.37, -14) * mm, "end": v(45.43, -13.94) * mm});
            skArc(sketch, "E274", {"start": v(44.8, -15.83) * mm, "mid": v(44.88, -15.63) * mm, "end": v(44.95, -15.43) * mm});
            skArc(sketch, "E275", {"start": v(44.27, -17.3) * mm, "mid": v(44.25, -17.2) * mm, "end": v(44.2, -17.13) * mm});
            skArc(sketch, "E276", {"start": v(44.2, -17.13) * mm, "mid": v(44.15, -17.08) * mm, "end": v(44.09, -17.04) * mm});
            skArc(sketch, "E277", {"start": v(44.5, -15.91) * mm, "mid": v(43.84, -16.3) * mm, "end": v(44.09, -17.04) * mm});
            skArc(sketch, "E278", {"start": v(44.5, -15.91) * mm, "mid": v(44.58, -15.92) * mm, "end": v(44.66, -15.91) * mm});
            skArc(sketch, "E279", {"start": v(44.66, -15.91) * mm, "mid": v(44.74, -15.89) * mm, "end": v(44.8, -15.83) * mm});
            skArc(sketch, "E280", {"start": v(44.1, -17.7) * mm, "mid": v(44.19, -17.5) * mm, "end": v(44.27, -17.3) * mm});
            skArc(sketch, "E281", {"start": v(43.5, -19.13) * mm, "mid": v(43.5, -19.04) * mm, "end": v(43.45, -18.97) * mm});
            skArc(sketch, "E282", {"start": v(43.45, -18.97) * mm, "mid": v(43.4, -18.91) * mm, "end": v(43.33, -18.87) * mm});
            skArc(sketch, "E283", {"start": v(43.8, -17.76) * mm, "mid": v(43.12, -18.13) * mm, "end": v(43.33, -18.87) * mm});
            skArc(sketch, "E284", {"start": v(43.8, -17.76) * mm, "mid": v(43.87, -17.77) * mm, "end": v(43.95, -17.77) * mm});
            skArc(sketch, "E285", {"start": v(43.95, -17.77) * mm, "mid": v(44.04, -17.75) * mm, "end": v(44.1, -17.7) * mm});
            skArc(sketch, "E286", {"start": v(43.33, -19.53) * mm, "mid": v(43.42, -19.33) * mm, "end": v(43.5, -19.13) * mm});
            skArc(sketch, "E287", {"start": v(42.66, -20.94) * mm, "mid": v(42.66, -20.85) * mm, "end": v(42.61, -20.77) * mm});
            skArc(sketch, "E288", {"start": v(42.61, -20.77) * mm, "mid": v(42.56, -20.71) * mm, "end": v(42.5, -20.66) * mm});
            skArc(sketch, "E289", {"start": v(43.02, -19.58) * mm, "mid": v(42.32, -19.92) * mm, "end": v(42.5, -20.66) * mm});
            skArc(sketch, "E290", {"start": v(43.02, -19.58) * mm, "mid": v(43.1, -19.6) * mm, "end": v(43.17, -19.6) * mm});
            skArc(sketch, "E291", {"start": v(43.17, -19.6) * mm, "mid": v(43.25, -19.58) * mm, "end": v(43.33, -19.53) * mm});
            skArc(sketch, "E292", {"start": v(42.47, -21.32) * mm, "mid": v(42.57, -21.13) * mm, "end": v(42.66, -20.94) * mm});
            skArc(sketch, "E293", {"start": v(41.75, -22.7) * mm, "mid": v(41.74, -22.62) * mm, "end": v(41.7, -22.54) * mm});
            skArc(sketch, "E294", {"start": v(41.7, -22.54) * mm, "mid": v(41.66, -22.48) * mm, "end": v(41.6, -22.43) * mm});
            skArc(sketch, "E295", {"start": v(42.16, -21.36) * mm, "mid": v(41.45, -21.67) * mm, "end": v(41.6, -22.43) * mm});
            skArc(sketch, "E296", {"start": v(42.16, -21.36) * mm, "mid": v(42.23, -21.38) * mm, "end": v(42.3, -21.38) * mm});
            skArc(sketch, "E297", {"start": v(42.3, -21.38) * mm, "mid": v(42.4, -21.37) * mm, "end": v(42.47, -21.32) * mm});
            skArc(sketch, "E298", {"start": v(41.54, -23.08) * mm, "mid": v(41.65, -22.9) * mm, "end": v(41.75, -22.7) * mm});
            skArc(sketch, "E299", {"start": v(40.76, -24.43) * mm, "mid": v(40.76, -24.35) * mm, "end": v(40.73, -24.26) * mm});
            skArc(sketch, "E300", {"start": v(40.73, -24.26) * mm, "mid": v(40.68, -24.2) * mm, "end": v(40.63, -24.15) * mm});
            skArc(sketch, "E301", {"start": v(41.23, -23.1) * mm, "mid": v(40.5, -23.39) * mm, "end": v(40.63, -24.15) * mm});
            skArc(sketch, "E302", {"start": v(41.23, -23.1) * mm, "mid": v(41.3, -23.13) * mm, "end": v(41.38, -23.14) * mm});
            skArc(sketch, "E303", {"start": v(41.38, -23.14) * mm, "mid": v(41.46, -23.13) * mm, "end": v(41.54, -23.08) * mm});
            skArc(sketch, "E304", {"start": v(40.54, -24.8) * mm, "mid": v(40.65, -24.62) * mm, "end": v(40.76, -24.43) * mm});
            skArc(sketch, "E305", {"start": v(39.7, -26.12) * mm, "mid": v(39.7, -26.03) * mm, "end": v(39.67, -25.95) * mm});
            skArc(sketch, "E306", {"start": v(39.67, -25.95) * mm, "mid": v(39.63, -25.89) * mm, "end": v(39.58, -25.83) * mm});
            skArc(sketch, "E307", {"start": v(40.22, -24.82) * mm, "mid": v(39.5, -25.06) * mm, "end": v(39.58, -25.83) * mm});
            skArc(sketch, "E308", {"start": v(40.22, -24.82) * mm, "mid": v(40.3, -24.84) * mm, "end": v(40.37, -24.85) * mm});
            skArc(sketch, "E309", {"start": v(40.37, -24.85) * mm, "mid": v(40.46, -24.84) * mm, "end": v(40.54, -24.8) * mm});
            skArc(sketch, "E310", {"start": v(39.46, -26.48) * mm, "mid": v(39.58, -26.3) * mm, "end": v(39.7, -26.12) * mm});
            skArc(sketch, "E311", {"start": v(38.58, -27.76) * mm, "mid": v(38.58, -27.67) * mm, "end": v(38.55, -27.59) * mm});
            skArc(sketch, "E312", {"start": v(38.55, -27.59) * mm, "mid": v(38.51, -27.52) * mm, "end": v(38.46, -27.46) * mm});
            skArc(sketch, "E313", {"start": v(39.15, -26.48) * mm, "mid": v(38.4, -26.7) * mm, "end": v(38.46, -27.46) * mm});
            skArc(sketch, "E314", {"start": v(39.15, -26.48) * mm, "mid": v(39.22, -26.5) * mm, "end": v(39.3, -26.52) * mm});
            skArc(sketch, "E315", {"start": v(39.3, -26.52) * mm, "mid": v(39.38, -26.52) * mm, "end": v(39.46, -26.48) * mm});
            skArc(sketch, "E316", {"start": v(38.32, -28.1) * mm, "mid": v(38.45, -27.93) * mm, "end": v(38.58, -27.76) * mm});
            skArc(sketch, "E317", {"start": v(37.38, -29.35) * mm, "mid": v(37.39, -29.26) * mm, "end": v(37.36, -29.18) * mm});
            skArc(sketch, "E318", {"start": v(37.36, -29.18) * mm, "mid": v(37.33, -29.11) * mm, "end": v(37.28, -29.05) * mm});
            skArc(sketch, "E319", {"start": v(38, -28.1) * mm, "mid": v(37.26, -28.28) * mm, "end": v(37.28, -29.05) * mm});
            skArc(sketch, "E320", {"start": v(38, -28.1) * mm, "mid": v(38.08, -28.12) * mm, "end": v(38.15, -28.14) * mm});
            skArc(sketch, "E321", {"start": v(38.15, -28.14) * mm, "mid": v(38.24, -28.14) * mm, "end": v(38.32, -28.1) * mm});
            skArc(sketch, "E322", {"start": v(37.11, -29.69) * mm, "mid": v(37.25, -29.52) * mm, "end": v(37.38, -29.35) * mm});
            skArc(sketch, "E323", {"start": v(36.12, -30.89) * mm, "mid": v(36.13, -30.8) * mm, "end": v(36.1, -30.72) * mm});
            skArc(sketch, "E324", {"start": v(36.1, -30.72) * mm, "mid": v(36.07, -30.65) * mm, "end": v(36.03, -30.59) * mm});
            skArc(sketch, "E325", {"start": v(36.8, -29.66) * mm, "mid": v(36.04, -29.82) * mm, "end": v(36.03, -30.59) * mm});
            skArc(sketch, "E326", {"start": v(36.8, -29.66) * mm, "mid": v(36.87, -29.7) * mm, "end": v(36.94, -29.71) * mm});
            skArc(sketch, "E327", {"start": v(36.94, -29.71) * mm, "mid": v(37.03, -29.72) * mm, "end": v(37.11, -29.69) * mm});
            skArc(sketch, "E328", {"start": v(35.83, -31.22) * mm, "mid": v(35.98, -31.05) * mm, "end": v(36.12, -30.89) * mm});
            skArc(sketch, "E329", {"start": v(34.8, -32.38) * mm, "mid": v(34.8, -32.29) * mm, "end": v(34.8, -32.2) * mm});
            skArc(sketch, "E330", {"start": v(34.8, -32.2) * mm, "mid": v(34.76, -32.13) * mm, "end": v(34.72, -32.07) * mm});
            skArc(sketch, "E331", {"start": v(35.52, -31.18) * mm, "mid": v(34.76, -31.3) * mm, "end": v(34.72, -32.07) * mm});
            skArc(sketch, "E332", {"start": v(35.52, -31.18) * mm, "mid": v(35.59, -31.2) * mm, "end": v(35.66, -31.24) * mm});
            skArc(sketch, "E333", {"start": v(35.66, -31.24) * mm, "mid": v(35.75, -31.24) * mm, "end": v(35.83, -31.22) * mm});
            skArc(sketch, "E334", {"start": v(34.5, -32.7) * mm, "mid": v(34.64, -32.53) * mm, "end": v(34.8, -32.38) * mm});
            skArc(sketch, "E335", {"start": v(33.4, -33.8) * mm, "mid": v(33.43, -33.72) * mm, "end": v(33.41, -33.63) * mm});
            skArc(sketch, "E336", {"start": v(33.41, -33.63) * mm, "mid": v(33.38, -33.56) * mm, "end": v(33.34, -33.5) * mm});
            skArc(sketch, "E337", {"start": v(34.18, -32.64) * mm, "mid": v(33.42, -32.73) * mm, "end": v(33.34, -33.5) * mm});
            skArc(sketch, "E338", {"start": v(34.18, -32.64) * mm, "mid": v(34.25, -32.67) * mm, "end": v(34.32, -32.7) * mm});
            skArc(sketch, "E339", {"start": v(34.32, -32.7) * mm, "mid": v(34.41, -32.71) * mm, "end": v(34.5, -32.7) * mm});
            skArc(sketch, "E340", {"start": v(33.1, -34.1) * mm, "mid": v(33.25, -33.96) * mm, "end": v(33.4, -33.8) * mm});
            skArc(sketch, "E341", {"start": v(31.96, -35.17) * mm, "mid": v(31.98, -35.09) * mm, "end": v(31.98, -35) * mm});
            skArc(sketch, "E342", {"start": v(31.98, -35) * mm, "mid": v(31.95, -34.93) * mm, "end": v(31.91, -34.86) * mm});
            skArc(sketch, "E343", {"start": v(32.79, -34.04) * mm, "mid": v(32.02, -34.1) * mm, "end": v(31.91, -34.86) * mm});
            skArc(sketch, "E344", {"start": v(32.79, -34.04) * mm, "mid": v(32.85, -34.08) * mm, "end": v(32.92, -34.1) * mm});
            skArc(sketch, "E345", {"start": v(32.92, -34.1) * mm, "mid": v(33.01, -34.12) * mm, "end": v(33.1, -34.1) * mm});
            skArc(sketch, "E346", {"start": v(31.64, -35.46) * mm, "mid": v(31.8, -35.32) * mm, "end": v(31.96, -35.17) * mm});
            skArc(sketch, "E347", {"start": v(30.46, -36.48) * mm, "mid": v(30.49, -36.4) * mm, "end": v(30.48, -36.3) * mm});
            skArc(sketch, "E348", {"start": v(30.48, -36.3) * mm, "mid": v(30.46, -36.24) * mm, "end": v(30.43, -36.17) * mm});
            skArc(sketch, "E349", {"start": v(31.33, -35.38) * mm, "mid": v(30.56, -35.4) * mm, "end": v(30.43, -36.17) * mm});
            skArc(sketch, "E350", {"start": v(31.33, -35.38) * mm, "mid": v(31.4, -35.42) * mm, "end": v(31.47, -35.46) * mm});
            skArc(sketch, "E351", {"start": v(31.47, -35.46) * mm, "mid": v(31.55, -35.48) * mm, "end": v(31.64, -35.46) * mm});
            skArc(sketch, "E352", {"start": v(30.13, -36.76) * mm, "mid": v(30.3, -36.62) * mm, "end": v(30.46, -36.48) * mm});
            skArc(sketch, "E353", {"start": v(28.9, -37.72) * mm, "mid": v(28.94, -37.64) * mm, "end": v(28.93, -37.55) * mm});
            skArc(sketch, "E354", {"start": v(28.93, -37.55) * mm, "mid": v(28.91, -37.48) * mm, "end": v(28.88, -37.4) * mm});
            skArc(sketch, "E355", {"start": v(29.82, -36.66) * mm, "mid": v(29.05, -36.66) * mm, "end": v(28.88, -37.4) * mm});
            skArc(sketch, "E356", {"start": v(29.82, -36.66) * mm, "mid": v(29.89, -36.7) * mm, "end": v(29.95, -36.74) * mm});
            skArc(sketch, "E357", {"start": v(29.95, -36.74) * mm, "mid": v(30.04, -36.77) * mm, "end": v(30.13, -36.76) * mm});
            skArc(sketch, "E358", {"start": v(28.56, -37.99) * mm, "mid": v(28.73, -37.86) * mm, "end": v(28.9, -37.72) * mm});
            skArc(sketch, "E359", {"start": v(27.3, -38.9) * mm, "mid": v(27.33, -38.82) * mm, "end": v(27.34, -38.73) * mm});
            skArc(sketch, "E360", {"start": v(27.34, -38.73) * mm, "mid": v(27.32, -38.66) * mm, "end": v(27.3, -38.59) * mm});
            skArc(sketch, "E361", {"start": v(28.26, -37.88) * mm, "mid": v(27.5, -37.84) * mm, "end": v(27.3, -38.59) * mm});
            skArc(sketch, "E362", {"start": v(28.26, -37.88) * mm, "mid": v(28.32, -37.93) * mm, "end": v(28.39, -37.97) * mm});
            skArc(sketch, "E363", {"start": v(28.39, -37.97) * mm, "mid": v(28.47, -38) * mm, "end": v(28.56, -37.99) * mm});
            skArc(sketch, "E364", {"start": v(26.95, -39.15) * mm, "mid": v(27.12, -39.03) * mm, "end": v(27.3, -38.9) * mm});
            skArc(sketch, "E365", {"start": v(25.65, -40.01) * mm, "mid": v(25.69, -39.93) * mm, "end": v(25.7, -39.84) * mm});
            skArc(sketch, "E366", {"start": v(25.7, -39.84) * mm, "mid": v(25.68, -39.77) * mm, "end": v(25.65, -39.7) * mm});
            skArc(sketch, "E367", {"start": v(26.65, -39.03) * mm, "mid": v(25.89, -38.96) * mm, "end": v(25.65, -39.7) * mm});
            skArc(sketch, "E368", {"start": v(26.65, -39.03) * mm, "mid": v(26.71, -39.08) * mm, "end": v(26.77, -39.12) * mm});
            skArc(sketch, "E369", {"start": v(26.77, -39.12) * mm, "mid": v(26.86, -39.15) * mm, "end": v(26.95, -39.15) * mm});
            skArc(sketch, "E370", {"start": v(25.28, -40.24) * mm, "mid": v(25.47, -40.13) * mm, "end": v(25.65, -40.01) * mm});
            skArc(sketch, "E371", {"start": v(23.95, -41.05) * mm, "mid": v(24, -40.97) * mm, "end": v(24, -40.88) * mm});
            skArc(sketch, "E372", {"start": v(24, -40.88) * mm, "mid": v(23.99, -40.8) * mm, "end": v(23.97, -40.73) * mm});
            skArc(sketch, "E373", {"start": v(25, -40.11) * mm, "mid": v(24.23, -40.01) * mm, "end": v(23.97, -40.73) * mm});
            skArc(sketch, "E374", {"start": v(25, -40.11) * mm, "mid": v(25.05, -40.16) * mm, "end": v(25.11, -40.2) * mm});
            skArc(sketch, "E375", {"start": v(25.11, -40.2) * mm, "mid": v(25.2, -40.24) * mm, "end": v(25.28, -40.24) * mm});
            skArc(sketch, "E376", {"start": v(23.58, -41.27) * mm, "mid": v(23.76, -41.16) * mm, "end": v(23.95, -41.05) * mm});
            skArc(sketch, "E377", {"start": v(22.2, -42.02) * mm, "mid": v(22.25, -41.94) * mm, "end": v(22.27, -41.85) * mm});
            skArc(sketch, "E378", {"start": v(22.27, -41.85) * mm, "mid": v(22.26, -41.78) * mm, "end": v(22.24, -41.7) * mm});
            skArc(sketch, "E379", {"start": v(23.3, -41.12) * mm, "mid": v(22.53, -40.99) * mm, "end": v(22.24, -41.7) * mm});
            skArc(sketch, "E380", {"start": v(23.3, -41.12) * mm, "mid": v(23.35, -41.18) * mm, "end": v(23.4, -41.23) * mm});
            skArc(sketch, "E381", {"start": v(23.4, -41.23) * mm, "mid": v(23.49, -41.26) * mm, "end": v(23.58, -41.27) * mm});
            skArc(sketch, "E382", {"start": v(21.83, -42.22) * mm, "mid": v(22.02, -42.12) * mm, "end": v(22.2, -42.02) * mm});
            skArc(sketch, "E383", {"start": v(20.43, -42.9) * mm, "mid": v(20.48, -42.83) * mm, "end": v(20.5, -42.75) * mm});
            skArc(sketch, "E384", {"start": v(20.5, -42.75) * mm, "mid": v(20.49, -42.67) * mm, "end": v(20.47, -42.6) * mm});
            skArc(sketch, "E385", {"start": v(21.55, -42.06) * mm, "mid": v(20.8, -41.9) * mm, "end": v(20.47, -42.6) * mm});
            skArc(sketch, "E386", {"start": v(21.55, -42.06) * mm, "mid": v(21.6, -42.12) * mm, "end": v(21.66, -42.17) * mm});
            skArc(sketch, "E387", {"start": v(21.66, -42.17) * mm, "mid": v(21.74, -42.2) * mm, "end": v(21.83, -42.22) * mm});
            skArc(sketch, "E388", {"start": v(20.04, -43.1) * mm, "mid": v(20.24, -43) * mm, "end": v(20.43, -42.9) * mm});
            skArc(sketch, "E389", {"start": v(18.62, -43.73) * mm, "mid": v(18.67, -43.65) * mm, "end": v(18.69, -43.57) * mm});
            skArc(sketch, "E390", {"start": v(18.69, -43.57) * mm, "mid": v(18.68, -43.5) * mm, "end": v(18.67, -43.42) * mm});
            skArc(sketch, "E391", {"start": v(19.77, -42.93) * mm, "mid": v(19.03, -42.73) * mm, "end": v(18.67, -43.42) * mm});
            skArc(sketch, "E392", {"start": v(19.77, -42.93) * mm, "mid": v(19.82, -42.99) * mm, "end": v(19.87, -43.04) * mm});
            skArc(sketch, "E393", {"start": v(19.87, -43.04) * mm, "mid": v(19.95, -43.08) * mm, "end": v(20.04, -43.1) * mm});
            skArc(sketch, "E394", {"start": v(18.22, -43.9) * mm, "mid": v(18.42, -43.81) * mm, "end": v(18.62, -43.73) * mm});
            skArc(sketch, "E395", {"start": v(16.77, -44.47) * mm, "mid": v(16.82, -44.4) * mm, "end": v(16.85, -44.31) * mm});
            skArc(sketch, "E396", {"start": v(16.85, -44.31) * mm, "mid": v(16.85, -44.24) * mm, "end": v(16.84, -44.16) * mm});
            skArc(sketch, "E397", {"start": v(17.96, -43.72) * mm, "mid": v(17.22, -43.5) * mm, "end": v(16.84, -44.16) * mm});
            skArc(sketch, "E398", {"start": v(17.96, -43.72) * mm, "mid": v(18, -43.78) * mm, "end": v(18.05, -43.83) * mm});
            skArc(sketch, "E399", {"start": v(18.05, -43.83) * mm, "mid": v(18.13, -43.88) * mm, "end": v(18.22, -43.9) * mm});
            skArc(sketch, "E400", {"start": v(16.36, -44.62) * mm, "mid": v(16.57, -44.54) * mm, "end": v(16.77, -44.47) * mm});
            skArc(sketch, "E401", {"start": v(14.9, -45.13) * mm, "mid": v(14.95, -45.06) * mm, "end": v(14.97, -44.98) * mm});
            skArc(sketch, "E402", {"start": v(14.97, -44.98) * mm, "mid": v(14.98, -44.9) * mm, "end": v(14.97, -44.83) * mm});
            skArc(sketch, "E403", {"start": v(16.1, -44.43) * mm, "mid": v(15.38, -44.17) * mm, "end": v(14.97, -44.83) * mm});
            skArc(sketch, "E404", {"start": v(16.1, -44.43) * mm, "mid": v(16.15, -44.5) * mm, "end": v(16.2, -44.55) * mm});
            skArc(sketch, "E405", {"start": v(16.2, -44.55) * mm, "mid": v(16.28, -44.6) * mm, "end": v(16.36, -44.62) * mm});
            skArc(sketch, "E406", {"start": v(14.48, -45.27) * mm, "mid": v(14.69, -45.2) * mm, "end": v(14.9, -45.13) * mm});
            skArc(sketch, "E407", {"start": v(12.99, -45.72) * mm, "mid": v(13.05, -45.65) * mm, "end": v(13.08, -45.57) * mm});
            skArc(sketch, "E408", {"start": v(13.08, -45.57) * mm, "mid": v(13.09, -45.5) * mm, "end": v(13.08, -45.41) * mm});
            skArc(sketch, "E409", {"start": v(14.23, -45.07) * mm, "mid": v(13.52, -44.78) * mm, "end": v(13.08, -45.41) * mm});
            skArc(sketch, "E410", {"start": v(14.23, -45.07) * mm, "mid": v(14.27, -45.13) * mm, "end": v(14.32, -45.2) * mm});
            skArc(sketch, "E411", {"start": v(14.32, -45.2) * mm, "mid": v(14.4, -45.24) * mm, "end": v(14.48, -45.27) * mm});
            skArc(sketch, "E412", {"start": v(12.57, -45.83) * mm, "mid": v(12.78, -45.77) * mm, "end": v(12.99, -45.72) * mm});
            skArc(sketch, "E413", {"start": v(11.06, -46.22) * mm, "mid": v(11.12, -46.16) * mm, "end": v(11.16, -46.07) * mm});
            skArc(sketch, "E414", {"start": v(11.16, -46.07) * mm, "mid": v(11.17, -46) * mm, "end": v(11.17, -45.92) * mm});
            skArc(sketch, "E415", {"start": v(12.33, -45.62) * mm, "mid": v(11.63, -45.3) * mm, "end": v(11.17, -45.92) * mm});
            skArc(sketch, "E416", {"start": v(12.33, -45.62) * mm, "mid": v(12.37, -45.7) * mm, "end": v(12.42, -45.75) * mm});
            skArc(sketch, "E417", {"start": v(12.42, -45.75) * mm, "mid": v(12.49, -45.8) * mm, "end": v(12.57, -45.83) * mm});
            skArc(sketch, "E418", {"start": v(10.64, -46.32) * mm, "mid": v(10.85, -46.27) * mm, "end": v(11.06, -46.22) * mm});
            skArc(sketch, "E419", {"start": v(9.12, -46.64) * mm, "mid": v(9.18, -46.58) * mm, "end": v(9.22, -46.5) * mm});
            skArc(sketch, "E420", {"start": v(9.22, -46.5) * mm, "mid": v(9.23, -46.43) * mm, "end": v(9.24, -46.35) * mm});
            skArc(sketch, "E421", {"start": v(10.41, -46.1) * mm, "mid": v(9.73, -45.75) * mm, "end": v(9.24, -46.35) * mm});
            skArc(sketch, "E422", {"start": v(10.41, -46.1) * mm, "mid": v(10.45, -46.17) * mm, "end": v(10.5, -46.23) * mm});
            skArc(sketch, "E423", {"start": v(10.5, -46.23) * mm, "mid": v(10.56, -46.29) * mm, "end": v(10.64, -46.32) * mm});
            skArc(sketch, "E424", {"start": v(8.7, -46.72) * mm, "mid": v(8.9, -46.68) * mm, "end": v(9.12, -46.64) * mm});
            skArc(sketch, "E425", {"start": v(7.16, -46.98) * mm, "mid": v(7.22, -46.93) * mm, "end": v(7.26, -46.85) * mm});
            skArc(sketch, "E426", {"start": v(7.26, -46.85) * mm, "mid": v(7.28, -46.77) * mm, "end": v(7.29, -46.7) * mm});
            skArc(sketch, "E427", {"start": v(8.47, -46.5) * mm, "mid": v(7.8, -46.12) * mm, "end": v(7.29, -46.7) * mm});
            skArc(sketch, "E428", {"start": v(8.47, -46.5) * mm, "mid": v(8.5, -46.57) * mm, "end": v(8.55, -46.63) * mm});
            skArc(sketch, "E429", {"start": v(8.55, -46.63) * mm, "mid": v(8.61, -46.7) * mm, "end": v(8.7, -46.72) * mm});
            skArc(sketch, "E430", {"start": v(6.73, -47.05) * mm, "mid": v(6.94, -47.02) * mm, "end": v(7.16, -46.98) * mm});
            skArc(sketch, "E431", {"start": v(5.18, -47.24) * mm, "mid": v(5.25, -47.19) * mm, "end": v(5.3, -47.1) * mm});
            skArc(sketch, "E432", {"start": v(5.3, -47.1) * mm, "mid": v(5.32, -47.04) * mm, "end": v(5.33, -46.96) * mm});
            skArc(sketch, "E433", {"start": v(6.52, -46.81) * mm, "mid": v(5.86, -46.4) * mm, "end": v(5.33, -46.96) * mm});
            skArc(sketch, "E434", {"start": v(6.52, -46.81) * mm, "mid": v(6.55, -46.88) * mm, "end": v(6.59, -46.95) * mm});
            skArc(sketch, "E435", {"start": v(6.59, -46.95) * mm, "mid": v(6.65, -47.01) * mm, "end": v(6.73, -47.05) * mm});
            skArc(sketch, "E436", {"start": v(4.75, -47.29) * mm, "mid": v(4.97, -47.26) * mm, "end": v(5.18, -47.24) * mm});
            skArc(sketch, "E437", {"start": v(3.2, -47.42) * mm, "mid": v(3.27, -47.37) * mm, "end": v(3.32, -47.3) * mm});
            skArc(sketch, "E438", {"start": v(3.32, -47.3) * mm, "mid": v(3.34, -47.22) * mm, "end": v(3.36, -47.14) * mm});
            skArc(sketch, "E439", {"start": v(4.55, -47.04) * mm, "mid": v(3.91, -46.61) * mm, "end": v(3.36, -47.14) * mm});
            skArc(sketch, "E440", {"start": v(4.55, -47.04) * mm, "mid": v(4.58, -47.11) * mm, "end": v(4.61, -47.18) * mm});
            skArc(sketch, "E441", {"start": v(4.61, -47.18) * mm, "mid": v(4.67, -47.25) * mm, "end": v(4.75, -47.29) * mm});
            skArc(sketch, "E442", {"start": v(2.77, -47.44) * mm, "mid": v(2.98, -47.43) * mm, "end": v(3.2, -47.42) * mm});
            skArc(sketch, "E443", {"start": v(1.21, -47.5) * mm, "mid": v(1.29, -47.46) * mm, "end": v(1.34, -47.39) * mm});
            skArc(sketch, "E444", {"start": v(1.34, -47.39) * mm, "mid": v(1.36, -47.32) * mm, "end": v(1.38, -47.24) * mm});
            skArc(sketch, "E445", {"start": v(2.58, -47.2) * mm, "mid": v(1.96, -46.73) * mm, "end": v(1.38, -47.24) * mm});
            skArc(sketch, "E446", {"start": v(2.58, -47.2) * mm, "mid": v(2.6, -47.26) * mm, "end": v(2.63, -47.33) * mm});
            skArc(sketch, "E447", {"start": v(2.63, -47.33) * mm, "mid": v(2.7, -47.4) * mm, "end": v(2.77, -47.44) * mm});
            skArc(sketch, "E448", {"start": v(0.78, -47.52) * mm, "mid": v(1, -47.51) * mm, "end": v(1.21, -47.5) * mm});
            skArc(sketch, "E449", {"start": v(-0.78, -47.52) * mm, "mid": v(-0.7, -47.47) * mm, "end": v(-0.65, -47.4) * mm});
            skArc(sketch, "E450", {"start": v(-0.65, -47.4) * mm, "mid": v(-0.62, -47.33) * mm, "end": v(-0.6, -47.26) * mm});
            skArc(sketch, "E451", {"start": v(0.6, -47.26) * mm, "mid": v(0, -46.78) * mm, "end": v(-0.6, -47.26) * mm});
            skArc(sketch, "E452", {"start": v(0.6, -47.26) * mm, "mid": v(0.62, -47.33) * mm, "end": v(0.65, -47.4) * mm});
            skArc(sketch, "E453", {"start": v(0.65, -47.4) * mm, "mid": v(0.7, -47.47) * mm, "end": v(0.78, -47.52) * mm});
            skArc(sketch, "E454", {"start": v(-1.21, -47.5) * mm, "mid": v(-1, -47.51) * mm, "end": v(-0.78, -47.52) * mm});
            skArc(sketch, "E455", {"start": v(-2.77, -47.44) * mm, "mid": v(-2.7, -47.4) * mm, "end": v(-2.63, -47.33) * mm});
            skArc(sketch, "E456", {"start": v(-2.63, -47.33) * mm, "mid": v(-2.6, -47.26) * mm, "end": v(-2.58, -47.2) * mm});
            skArc(sketch, "E457", {"start": v(-1.38, -47.24) * mm, "mid": v(-1.96, -46.73) * mm, "end": v(-2.58, -47.2) * mm});
            skArc(sketch, "E458", {"start": v(-1.38, -47.24) * mm, "mid": v(-1.36, -47.32) * mm, "end": v(-1.34, -47.39) * mm});
            skArc(sketch, "E459", {"start": v(-1.34, -47.39) * mm, "mid": v(-1.29, -47.46) * mm, "end": v(-1.21, -47.5) * mm});
            skArc(sketch, "E460", {"start": v(-3.2, -47.42) * mm, "mid": v(-2.98, -47.43) * mm, "end": v(-2.77, -47.44) * mm});
            skArc(sketch, "E461", {"start": v(-4.75, -47.29) * mm, "mid": v(-4.67, -47.25) * mm, "end": v(-4.61, -47.18) * mm});
            skArc(sketch, "E462", {"start": v(-4.61, -47.18) * mm, "mid": v(-4.58, -47.11) * mm, "end": v(-4.55, -47.04) * mm});
            skArc(sketch, "E463", {"start": v(-3.36, -47.14) * mm, "mid": v(-3.91, -46.61) * mm, "end": v(-4.55, -47.04) * mm});
            skArc(sketch, "E464", {"start": v(-3.36, -47.14) * mm, "mid": v(-3.34, -47.22) * mm, "end": v(-3.32, -47.3) * mm});
            skArc(sketch, "E465", {"start": v(-3.32, -47.3) * mm, "mid": v(-3.27, -47.37) * mm, "end": v(-3.2, -47.42) * mm});
            skArc(sketch, "E466", {"start": v(-5.18, -47.24) * mm, "mid": v(-4.97, -47.26) * mm, "end": v(-4.75, -47.29) * mm});
            skArc(sketch, "E467", {"start": v(-6.73, -47.05) * mm, "mid": v(-6.65, -47.01) * mm, "end": v(-6.59, -46.95) * mm});
            skArc(sketch, "E468", {"start": v(-6.59, -46.95) * mm, "mid": v(-6.55, -46.88) * mm, "end": v(-6.52, -46.81) * mm});
            skArc(sketch, "E469", {"start": v(-5.33, -46.96) * mm, "mid": v(-5.86, -46.4) * mm, "end": v(-6.52, -46.81) * mm});
            skArc(sketch, "E470", {"start": v(-5.33, -46.96) * mm, "mid": v(-5.32, -47.04) * mm, "end": v(-5.3, -47.1) * mm});
            skArc(sketch, "E471", {"start": v(-5.3, -47.1) * mm, "mid": v(-5.25, -47.19) * mm, "end": v(-5.18, -47.24) * mm});
            skArc(sketch, "E472", {"start": v(-7.16, -46.98) * mm, "mid": v(-6.94, -47.02) * mm, "end": v(-6.73, -47.05) * mm});
            skArc(sketch, "E473", {"start": v(-8.7, -46.72) * mm, "mid": v(-8.61, -46.7) * mm, "end": v(-8.55, -46.63) * mm});
            skArc(sketch, "E474", {"start": v(-8.55, -46.63) * mm, "mid": v(-8.5, -46.57) * mm, "end": v(-8.47, -46.5) * mm});
            skArc(sketch, "E475", {"start": v(-7.29, -46.7) * mm, "mid": v(-7.8, -46.12) * mm, "end": v(-8.47, -46.5) * mm});
            skArc(sketch, "E476", {"start": v(-7.29, -46.7) * mm, "mid": v(-7.28, -46.77) * mm, "end": v(-7.26, -46.85) * mm});
            skArc(sketch, "E477", {"start": v(-7.26, -46.85) * mm, "mid": v(-7.22, -46.93) * mm, "end": v(-7.16, -46.98) * mm});
            skArc(sketch, "E478", {"start": v(-9.12, -46.64) * mm, "mid": v(-8.9, -46.68) * mm, "end": v(-8.7, -46.72) * mm});
            skArc(sketch, "E479", {"start": v(-10.64, -46.32) * mm, "mid": v(-10.56, -46.29) * mm, "end": v(-10.5, -46.23) * mm});
            skArc(sketch, "E480", {"start": v(-10.5, -46.23) * mm, "mid": v(-10.45, -46.17) * mm, "end": v(-10.41, -46.1) * mm});
            skArc(sketch, "E481", {"start": v(-9.24, -46.35) * mm, "mid": v(-9.73, -45.75) * mm, "end": v(-10.41, -46.1) * mm});
            skArc(sketch, "E482", {"start": v(-9.24, -46.35) * mm, "mid": v(-9.23, -46.43) * mm, "end": v(-9.22, -46.5) * mm});
            skArc(sketch, "E483", {"start": v(-9.22, -46.5) * mm, "mid": v(-9.18, -46.58) * mm, "end": v(-9.12, -46.64) * mm});
            skArc(sketch, "E484", {"start": v(-11.06, -46.22) * mm, "mid": v(-10.85, -46.27) * mm, "end": v(-10.64, -46.32) * mm});
            skArc(sketch, "E485", {"start": v(-12.57, -45.83) * mm, "mid": v(-12.49, -45.8) * mm, "end": v(-12.42, -45.75) * mm});
            skArc(sketch, "E486", {"start": v(-12.42, -45.75) * mm, "mid": v(-12.37, -45.7) * mm, "end": v(-12.33, -45.62) * mm});
            skArc(sketch, "E487", {"start": v(-11.17, -45.92) * mm, "mid": v(-11.63, -45.3) * mm, "end": v(-12.33, -45.62) * mm});
            skArc(sketch, "E488", {"start": v(-11.17, -45.92) * mm, "mid": v(-11.17, -46) * mm, "end": v(-11.16, -46.07) * mm});
            skArc(sketch, "E489", {"start": v(-11.16, -46.07) * mm, "mid": v(-11.12, -46.16) * mm, "end": v(-11.06, -46.22) * mm});
            skArc(sketch, "E490", {"start": v(-12.99, -45.72) * mm, "mid": v(-12.78, -45.77) * mm, "end": v(-12.57, -45.83) * mm});
            skArc(sketch, "E491", {"start": v(-14.48, -45.27) * mm, "mid": v(-14.4, -45.24) * mm, "end": v(-14.32, -45.2) * mm});
            skArc(sketch, "E492", {"start": v(-14.32, -45.2) * mm, "mid": v(-14.27, -45.13) * mm, "end": v(-14.23, -45.07) * mm});
            skArc(sketch, "E493", {"start": v(-13.08, -45.41) * mm, "mid": v(-13.52, -44.78) * mm, "end": v(-14.23, -45.07) * mm});
            skArc(sketch, "E494", {"start": v(-13.08, -45.41) * mm, "mid": v(-13.09, -45.5) * mm, "end": v(-13.08, -45.57) * mm});
            skArc(sketch, "E495", {"start": v(-13.08, -45.57) * mm, "mid": v(-13.05, -45.65) * mm, "end": v(-12.99, -45.72) * mm});
            skArc(sketch, "E496", {"start": v(-14.9, -45.13) * mm, "mid": v(-14.69, -45.2) * mm, "end": v(-14.48, -45.27) * mm});
            skArc(sketch, "E497", {"start": v(-16.36, -44.62) * mm, "mid": v(-16.28, -44.6) * mm, "end": v(-16.2, -44.55) * mm});
            skArc(sketch, "E498", {"start": v(-16.2, -44.55) * mm, "mid": v(-16.15, -44.5) * mm, "end": v(-16.1, -44.43) * mm});
            skArc(sketch, "E499", {"start": v(-14.97, -44.83) * mm, "mid": v(-15.38, -44.17) * mm, "end": v(-16.1, -44.43) * mm});
            skArc(sketch, "E500", {"start": v(-14.97, -44.83) * mm, "mid": v(-14.98, -44.9) * mm, "end": v(-14.97, -44.98) * mm});
            skArc(sketch, "E501", {"start": v(-14.97, -44.98) * mm, "mid": v(-14.95, -45.06) * mm, "end": v(-14.9, -45.13) * mm});
            skArc(sketch, "E502", {"start": v(-16.77, -44.47) * mm, "mid": v(-16.57, -44.54) * mm, "end": v(-16.36, -44.62) * mm});
            skArc(sketch, "E503", {"start": v(-18.22, -43.9) * mm, "mid": v(-18.13, -43.88) * mm, "end": v(-18.05, -43.83) * mm});
            skArc(sketch, "E504", {"start": v(-18.05, -43.83) * mm, "mid": v(-18, -43.78) * mm, "end": v(-17.96, -43.72) * mm});
            skArc(sketch, "E505", {"start": v(-16.84, -44.16) * mm, "mid": v(-17.22, -43.5) * mm, "end": v(-17.96, -43.72) * mm});
            skArc(sketch, "E506", {"start": v(-16.84, -44.16) * mm, "mid": v(-16.85, -44.24) * mm, "end": v(-16.85, -44.31) * mm});
            skArc(sketch, "E507", {"start": v(-16.85, -44.31) * mm, "mid": v(-16.82, -44.4) * mm, "end": v(-16.77, -44.47) * mm});
            skArc(sketch, "E508", {"start": v(-18.62, -43.73) * mm, "mid": v(-18.42, -43.81) * mm, "end": v(-18.22, -43.9) * mm});
            skArc(sketch, "E509", {"start": v(-20.04, -43.1) * mm, "mid": v(-19.95, -43.08) * mm, "end": v(-19.87, -43.04) * mm});
            skArc(sketch, "E510", {"start": v(-19.87, -43.04) * mm, "mid": v(-19.82, -42.99) * mm, "end": v(-19.77, -42.93) * mm});
            skArc(sketch, "E511", {"start": v(-18.67, -43.42) * mm, "mid": v(-19.03, -42.73) * mm, "end": v(-19.77, -42.93) * mm});
            skArc(sketch, "E512", {"start": v(-18.67, -43.42) * mm, "mid": v(-18.68, -43.5) * mm, "end": v(-18.69, -43.57) * mm});
            skArc(sketch, "E513", {"start": v(-18.69, -43.57) * mm, "mid": v(-18.67, -43.65) * mm, "end": v(-18.62, -43.73) * mm});
            skArc(sketch, "E514", {"start": v(-20.43, -42.9) * mm, "mid": v(-20.24, -43) * mm, "end": v(-20.04, -43.1) * mm});
            skArc(sketch, "E515", {"start": v(-21.83, -42.22) * mm, "mid": v(-21.74, -42.2) * mm, "end": v(-21.66, -42.17) * mm});
            skArc(sketch, "E516", {"start": v(-21.66, -42.17) * mm, "mid": v(-21.6, -42.12) * mm, "end": v(-21.55, -42.06) * mm});
            skArc(sketch, "E517", {"start": v(-20.47, -42.6) * mm, "mid": v(-20.8, -41.9) * mm, "end": v(-21.55, -42.06) * mm});
            skArc(sketch, "E518", {"start": v(-20.47, -42.6) * mm, "mid": v(-20.49, -42.67) * mm, "end": v(-20.5, -42.75) * mm});
            skArc(sketch, "E519", {"start": v(-20.5, -42.75) * mm, "mid": v(-20.48, -42.83) * mm, "end": v(-20.43, -42.9) * mm});
            skArc(sketch, "E520", {"start": v(-22.2, -42.02) * mm, "mid": v(-22.02, -42.12) * mm, "end": v(-21.83, -42.22) * mm});
            skArc(sketch, "E521", {"start": v(-23.58, -41.27) * mm, "mid": v(-23.49, -41.26) * mm, "end": v(-23.4, -41.23) * mm});
            skArc(sketch, "E522", {"start": v(-23.4, -41.23) * mm, "mid": v(-23.35, -41.18) * mm, "end": v(-23.3, -41.12) * mm});
            skArc(sketch, "E523", {"start": v(-22.24, -41.7) * mm, "mid": v(-22.53, -40.99) * mm, "end": v(-23.3, -41.12) * mm});
            skArc(sketch, "E524", {"start": v(-22.24, -41.7) * mm, "mid": v(-22.26, -41.78) * mm, "end": v(-22.27, -41.85) * mm});
            skArc(sketch, "E525", {"start": v(-22.27, -41.85) * mm, "mid": v(-22.25, -41.94) * mm, "end": v(-22.2, -42.02) * mm});
            skArc(sketch, "E526", {"start": v(-23.95, -41.05) * mm, "mid": v(-23.76, -41.16) * mm, "end": v(-23.58, -41.27) * mm});
            skArc(sketch, "E527", {"start": v(-25.28, -40.24) * mm, "mid": v(-25.2, -40.24) * mm, "end": v(-25.11, -40.2) * mm});
            skArc(sketch, "E528", {"start": v(-25.11, -40.2) * mm, "mid": v(-25.05, -40.16) * mm, "end": v(-25, -40.11) * mm});
            skArc(sketch, "E529", {"start": v(-23.97, -40.73) * mm, "mid": v(-24.23, -40.01) * mm, "end": v(-25, -40.11) * mm});
            skArc(sketch, "E530", {"start": v(-23.97, -40.73) * mm, "mid": v(-23.99, -40.8) * mm, "end": v(-24, -40.88) * mm});
            skArc(sketch, "E531", {"start": v(-24, -40.88) * mm, "mid": v(-24, -40.97) * mm, "end": v(-23.95, -41.05) * mm});
            skArc(sketch, "E532", {"start": v(-25.65, -40.01) * mm, "mid": v(-25.47, -40.13) * mm, "end": v(-25.28, -40.24) * mm});
            skArc(sketch, "E533", {"start": v(-26.95, -39.15) * mm, "mid": v(-26.86, -39.15) * mm, "end": v(-26.77, -39.12) * mm});
            skArc(sketch, "E534", {"start": v(-26.77, -39.12) * mm, "mid": v(-26.71, -39.08) * mm, "end": v(-26.65, -39.03) * mm});
            skArc(sketch, "E535", {"start": v(-25.65, -39.7) * mm, "mid": v(-25.89, -38.96) * mm, "end": v(-26.65, -39.03) * mm});
            skArc(sketch, "E536", {"start": v(-25.65, -39.7) * mm, "mid": v(-25.68, -39.77) * mm, "end": v(-25.7, -39.84) * mm});
            skArc(sketch, "E537", {"start": v(-25.7, -39.84) * mm, "mid": v(-25.69, -39.93) * mm, "end": v(-25.65, -40.01) * mm});
            skArc(sketch, "E538", {"start": v(-27.3, -38.9) * mm, "mid": v(-27.12, -39.03) * mm, "end": v(-26.95, -39.15) * mm});
            skArc(sketch, "E539", {"start": v(-28.56, -37.99) * mm, "mid": v(-28.47, -38) * mm, "end": v(-28.39, -37.97) * mm});
            skArc(sketch, "E540", {"start": v(-28.39, -37.97) * mm, "mid": v(-28.32, -37.93) * mm, "end": v(-28.26, -37.88) * mm});
            skArc(sketch, "E541", {"start": v(-27.3, -38.59) * mm, "mid": v(-27.5, -37.84) * mm, "end": v(-28.26, -37.88) * mm});
            skArc(sketch, "E542", {"start": v(-27.3, -38.59) * mm, "mid": v(-27.32, -38.66) * mm, "end": v(-27.34, -38.73) * mm});
            skArc(sketch, "E543", {"start": v(-27.34, -38.73) * mm, "mid": v(-27.33, -38.82) * mm, "end": v(-27.3, -38.9) * mm});
            skArc(sketch, "E544", {"start": v(-28.9, -37.72) * mm, "mid": v(-28.73, -37.86) * mm, "end": v(-28.56, -37.99) * mm});
            skArc(sketch, "E545", {"start": v(-30.13, -36.76) * mm, "mid": v(-30.04, -36.77) * mm, "end": v(-29.95, -36.74) * mm});
            skArc(sketch, "E546", {"start": v(-29.95, -36.74) * mm, "mid": v(-29.89, -36.7) * mm, "end": v(-29.82, -36.66) * mm});
            skArc(sketch, "E547", {"start": v(-28.88, -37.4) * mm, "mid": v(-29.05, -36.66) * mm, "end": v(-29.82, -36.66) * mm});
            skArc(sketch, "E548", {"start": v(-28.88, -37.4) * mm, "mid": v(-28.91, -37.48) * mm, "end": v(-28.93, -37.55) * mm});
            skArc(sketch, "E549", {"start": v(-28.93, -37.55) * mm, "mid": v(-28.94, -37.64) * mm, "end": v(-28.9, -37.72) * mm});
            skArc(sketch, "E550", {"start": v(-30.46, -36.48) * mm, "mid": v(-30.3, -36.62) * mm, "end": v(-30.13, -36.76) * mm});
            skArc(sketch, "E551", {"start": v(-31.64, -35.46) * mm, "mid": v(-31.55, -35.48) * mm, "end": v(-31.47, -35.46) * mm});
            skArc(sketch, "E552", {"start": v(-31.47, -35.46) * mm, "mid": v(-31.4, -35.42) * mm, "end": v(-31.33, -35.38) * mm});
            skArc(sketch, "E553", {"start": v(-30.43, -36.17) * mm, "mid": v(-30.56, -35.4) * mm, "end": v(-31.33, -35.38) * mm});
            skArc(sketch, "E554", {"start": v(-30.43, -36.17) * mm, "mid": v(-30.46, -36.24) * mm, "end": v(-30.48, -36.3) * mm});
            skArc(sketch, "E555", {"start": v(-30.48, -36.3) * mm, "mid": v(-30.49, -36.4) * mm, "end": v(-30.46, -36.48) * mm});
            skArc(sketch, "E556", {"start": v(-31.96, -35.17) * mm, "mid": v(-31.8, -35.32) * mm, "end": v(-31.64, -35.46) * mm});
            skArc(sketch, "E557", {"start": v(-33.1, -34.1) * mm, "mid": v(-33.01, -34.12) * mm, "end": v(-32.92, -34.1) * mm});
            skArc(sketch, "E558", {"start": v(-32.92, -34.1) * mm, "mid": v(-32.85, -34.08) * mm, "end": v(-32.79, -34.04) * mm});
            skArc(sketch, "E559", {"start": v(-31.91, -34.86) * mm, "mid": v(-32.02, -34.1) * mm, "end": v(-32.79, -34.04) * mm});
            skArc(sketch, "E560", {"start": v(-31.91, -34.86) * mm, "mid": v(-31.95, -34.93) * mm, "end": v(-31.98, -35) * mm});
            skArc(sketch, "E561", {"start": v(-31.98, -35) * mm, "mid": v(-31.98, -35.09) * mm, "end": v(-31.96, -35.17) * mm});
            skArc(sketch, "E562", {"start": v(-33.4, -33.8) * mm, "mid": v(-33.25, -33.96) * mm, "end": v(-33.1, -34.1) * mm});
            skArc(sketch, "E563", {"start": v(-34.5, -32.7) * mm, "mid": v(-34.41, -32.71) * mm, "end": v(-34.32, -32.7) * mm});
            skArc(sketch, "E564", {"start": v(-34.32, -32.7) * mm, "mid": v(-34.25, -32.67) * mm, "end": v(-34.18, -32.64) * mm});
            skArc(sketch, "E565", {"start": v(-33.34, -33.5) * mm, "mid": v(-33.42, -32.73) * mm, "end": v(-34.18, -32.64) * mm});
            skArc(sketch, "E566", {"start": v(-33.34, -33.5) * mm, "mid": v(-33.38, -33.56) * mm, "end": v(-33.41, -33.63) * mm});
            skArc(sketch, "E567", {"start": v(-33.41, -33.63) * mm, "mid": v(-33.43, -33.72) * mm, "end": v(-33.4, -33.8) * mm});
            skArc(sketch, "E568", {"start": v(-34.8, -32.38) * mm, "mid": v(-34.64, -32.53) * mm, "end": v(-34.5, -32.7) * mm});
            skArc(sketch, "E569", {"start": v(-35.83, -31.22) * mm, "mid": v(-35.75, -31.24) * mm, "end": v(-35.66, -31.24) * mm});
            skArc(sketch, "E570", {"start": v(-35.66, -31.24) * mm, "mid": v(-35.59, -31.2) * mm, "end": v(-35.52, -31.18) * mm});
            skArc(sketch, "E571", {"start": v(-34.72, -32.07) * mm, "mid": v(-34.76, -31.3) * mm, "end": v(-35.52, -31.18) * mm});
            skArc(sketch, "E572", {"start": v(-34.72, -32.07) * mm, "mid": v(-34.76, -32.13) * mm, "end": v(-34.8, -32.2) * mm});
            skArc(sketch, "E573", {"start": v(-34.8, -32.2) * mm, "mid": v(-34.8, -32.29) * mm, "end": v(-34.8, -32.38) * mm});
            skArc(sketch, "E574", {"start": v(-36.12, -30.89) * mm, "mid": v(-35.98, -31.05) * mm, "end": v(-35.83, -31.22) * mm});
            skArc(sketch, "E575", {"start": v(-37.11, -29.69) * mm, "mid": v(-37.03, -29.72) * mm, "end": v(-36.94, -29.71) * mm});
            skArc(sketch, "E576", {"start": v(-36.94, -29.71) * mm, "mid": v(-36.87, -29.7) * mm, "end": v(-36.8, -29.66) * mm});
            skArc(sketch, "E577", {"start": v(-36.03, -30.59) * mm, "mid": v(-36.04, -29.82) * mm, "end": v(-36.8, -29.66) * mm});
            skArc(sketch, "E578", {"start": v(-36.03, -30.59) * mm, "mid": v(-36.07, -30.65) * mm, "end": v(-36.1, -30.72) * mm});
            skArc(sketch, "E579", {"start": v(-36.1, -30.72) * mm, "mid": v(-36.13, -30.8) * mm, "end": v(-36.12, -30.89) * mm});
            skArc(sketch, "E580", {"start": v(-37.38, -29.35) * mm, "mid": v(-37.25, -29.52) * mm, "end": v(-37.11, -29.69) * mm});
            skArc(sketch, "E581", {"start": v(-38.32, -28.1) * mm, "mid": v(-38.24, -28.14) * mm, "end": v(-38.15, -28.14) * mm});
            skArc(sketch, "E582", {"start": v(-38.15, -28.14) * mm, "mid": v(-38.08, -28.12) * mm, "end": v(-38, -28.1) * mm});
            skArc(sketch, "E583", {"start": v(-37.28, -29.05) * mm, "mid": v(-37.26, -28.28) * mm, "end": v(-38, -28.1) * mm});
            skArc(sketch, "E584", {"start": v(-37.28, -29.05) * mm, "mid": v(-37.33, -29.11) * mm, "end": v(-37.36, -29.18) * mm});
            skArc(sketch, "E585", {"start": v(-37.36, -29.18) * mm, "mid": v(-37.39, -29.26) * mm, "end": v(-37.38, -29.35) * mm});
            skArc(sketch, "E586", {"start": v(-38.58, -27.76) * mm, "mid": v(-38.45, -27.93) * mm, "end": v(-38.32, -28.1) * mm});
            skArc(sketch, "E587", {"start": v(-39.46, -26.48) * mm, "mid": v(-39.38, -26.52) * mm, "end": v(-39.3, -26.52) * mm});
            skArc(sketch, "E588", {"start": v(-39.3, -26.52) * mm, "mid": v(-39.22, -26.5) * mm, "end": v(-39.15, -26.48) * mm});
            skArc(sketch, "E589", {"start": v(-38.46, -27.46) * mm, "mid": v(-38.4, -26.7) * mm, "end": v(-39.15, -26.48) * mm});
            skArc(sketch, "E590", {"start": v(-38.46, -27.46) * mm, "mid": v(-38.51, -27.52) * mm, "end": v(-38.55, -27.59) * mm});
            skArc(sketch, "E591", {"start": v(-38.55, -27.59) * mm, "mid": v(-38.58, -27.67) * mm, "end": v(-38.58, -27.76) * mm});
            skArc(sketch, "E592", {"start": v(-39.7, -26.12) * mm, "mid": v(-39.58, -26.3) * mm, "end": v(-39.46, -26.48) * mm});
            skArc(sketch, "E593", {"start": v(-40.54, -24.8) * mm, "mid": v(-40.46, -24.84) * mm, "end": v(-40.37, -24.85) * mm});
            skArc(sketch, "E594", {"start": v(-40.37, -24.85) * mm, "mid": v(-40.3, -24.84) * mm, "end": v(-40.22, -24.82) * mm});
            skArc(sketch, "E595", {"start": v(-39.58, -25.83) * mm, "mid": v(-39.5, -25.06) * mm, "end": v(-40.22, -24.82) * mm});
            skArc(sketch, "E596", {"start": v(-39.58, -25.83) * mm, "mid": v(-39.63, -25.89) * mm, "end": v(-39.67, -25.95) * mm});
            skArc(sketch, "E597", {"start": v(-39.67, -25.95) * mm, "mid": v(-39.7, -26.03) * mm, "end": v(-39.7, -26.12) * mm});
            skArc(sketch, "E598", {"start": v(-40.76, -24.43) * mm, "mid": v(-40.65, -24.62) * mm, "end": v(-40.54, -24.8) * mm});
            skArc(sketch, "E599", {"start": v(-41.54, -23.08) * mm, "mid": v(-41.46, -23.13) * mm, "end": v(-41.38, -23.14) * mm});
            skArc(sketch, "E600", {"start": v(-41.38, -23.14) * mm, "mid": v(-41.3, -23.13) * mm, "end": v(-41.23, -23.1) * mm});
            skArc(sketch, "E601", {"start": v(-40.63, -24.15) * mm, "mid": v(-40.5, -23.39) * mm, "end": v(-41.23, -23.1) * mm});
            skArc(sketch, "E602", {"start": v(-40.63, -24.15) * mm, "mid": v(-40.68, -24.2) * mm, "end": v(-40.73, -24.26) * mm});
            skArc(sketch, "E603", {"start": v(-40.73, -24.26) * mm, "mid": v(-40.76, -24.35) * mm, "end": v(-40.76, -24.43) * mm});
            skArc(sketch, "E604", {"start": v(-41.75, -22.7) * mm, "mid": v(-41.65, -22.9) * mm, "end": v(-41.54, -23.08) * mm});
            skArc(sketch, "E605", {"start": v(-42.47, -21.32) * mm, "mid": v(-42.4, -21.37) * mm, "end": v(-42.3, -21.38) * mm});
            skArc(sketch, "E606", {"start": v(-42.3, -21.38) * mm, "mid": v(-42.23, -21.38) * mm, "end": v(-42.16, -21.36) * mm});
            skArc(sketch, "E607", {"start": v(-41.6, -22.43) * mm, "mid": v(-41.45, -21.67) * mm, "end": v(-42.16, -21.36) * mm});
            skArc(sketch, "E608", {"start": v(-41.6, -22.43) * mm, "mid": v(-41.66, -22.48) * mm, "end": v(-41.7, -22.54) * mm});
            skArc(sketch, "E609", {"start": v(-41.7, -22.54) * mm, "mid": v(-41.74, -22.62) * mm, "end": v(-41.75, -22.7) * mm});
            skArc(sketch, "E610", {"start": v(-42.66, -20.94) * mm, "mid": v(-42.57, -21.13) * mm, "end": v(-42.47, -21.32) * mm});
            skArc(sketch, "E611", {"start": v(-43.33, -19.53) * mm, "mid": v(-43.25, -19.58) * mm, "end": v(-43.17, -19.6) * mm});
            skArc(sketch, "E612", {"start": v(-43.17, -19.6) * mm, "mid": v(-43.1, -19.6) * mm, "end": v(-43.02, -19.58) * mm});
            skArc(sketch, "E613", {"start": v(-42.5, -20.66) * mm, "mid": v(-42.32, -19.92) * mm, "end": v(-43.02, -19.58) * mm});
            skArc(sketch, "E614", {"start": v(-42.5, -20.66) * mm, "mid": v(-42.56, -20.71) * mm, "end": v(-42.61, -20.77) * mm});
            skArc(sketch, "E615", {"start": v(-42.61, -20.77) * mm, "mid": v(-42.66, -20.85) * mm, "end": v(-42.66, -20.94) * mm});
            skArc(sketch, "E616", {"start": v(-43.5, -19.13) * mm, "mid": v(-43.42, -19.33) * mm, "end": v(-43.33, -19.53) * mm});
            skArc(sketch, "E617", {"start": v(-44.1, -17.7) * mm, "mid": v(-44.04, -17.75) * mm, "end": v(-43.95, -17.77) * mm});
            skArc(sketch, "E618", {"start": v(-43.95, -17.77) * mm, "mid": v(-43.87, -17.77) * mm, "end": v(-43.8, -17.76) * mm});
            skArc(sketch, "E619", {"start": v(-43.33, -18.87) * mm, "mid": v(-43.12, -18.13) * mm, "end": v(-43.8, -17.76) * mm});
            skArc(sketch, "E620", {"start": v(-43.33, -18.87) * mm, "mid": v(-43.4, -18.91) * mm, "end": v(-43.45, -18.97) * mm});
            skArc(sketch, "E621", {"start": v(-43.45, -18.97) * mm, "mid": v(-43.5, -19.04) * mm, "end": v(-43.5, -19.13) * mm});
            skArc(sketch, "E622", {"start": v(-44.27, -17.3) * mm, "mid": v(-44.19, -17.5) * mm, "end": v(-44.1, -17.7) * mm});
            skArc(sketch, "E623", {"start": v(-44.8, -15.83) * mm, "mid": v(-44.74, -15.89) * mm, "end": v(-44.66, -15.91) * mm});
            skArc(sketch, "E624", {"start": v(-44.66, -15.91) * mm, "mid": v(-44.58, -15.92) * mm, "end": v(-44.5, -15.91) * mm});
            skArc(sketch, "E625", {"start": v(-44.09, -17.04) * mm, "mid": v(-43.84, -16.3) * mm, "end": v(-44.5, -15.91) * mm});
            skArc(sketch, "E626", {"start": v(-44.09, -17.04) * mm, "mid": v(-44.15, -17.08) * mm, "end": v(-44.2, -17.13) * mm});
            skArc(sketch, "E627", {"start": v(-44.2, -17.13) * mm, "mid": v(-44.25, -17.2) * mm, "end": v(-44.27, -17.3) * mm});
            skArc(sketch, "E628", {"start": v(-44.95, -15.43) * mm, "mid": v(-44.88, -15.63) * mm, "end": v(-44.8, -15.83) * mm});
            skArc(sketch, "E629", {"start": v(-45.43, -13.94) * mm, "mid": v(-45.37, -14) * mm, "end": v(-45.28, -14.03) * mm});
            skArc(sketch, "E630", {"start": v(-45.28, -14.03) * mm, "mid": v(-45.2, -14.04) * mm, "end": v(-45.13, -14.03) * mm});
            skArc(sketch, "E631", {"start": v(-44.76, -15.17) * mm, "mid": v(-44.49, -14.45) * mm, "end": v(-45.13, -14.03) * mm});
            skArc(sketch, "E632", {"start": v(-44.76, -15.17) * mm, "mid": v(-44.82, -15.22) * mm, "end": v(-44.88, -15.27) * mm});
            skArc(sketch, "E633", {"start": v(-44.88, -15.27) * mm, "mid": v(-44.93, -15.34) * mm, "end": v(-44.95, -15.43) * mm});
            skArc(sketch, "E634", {"start": v(-45.56, -13.53) * mm, "mid": v(-45.5, -13.74) * mm, "end": v(-45.43, -13.94) * mm});
            skArc(sketch, "E635", {"start": v(-45.98, -12.03) * mm, "mid": v(-45.91, -12.09) * mm, "end": v(-45.83, -12.12) * mm});
            skArc(sketch, "E636", {"start": v(-45.83, -12.12) * mm, "mid": v(-45.76, -12.13) * mm, "end": v(-45.68, -12.13) * mm});
            skArc(sketch, "E637", {"start": v(-45.36, -13.29) * mm, "mid": v(-45.05, -12.58) * mm, "end": v(-45.68, -12.13) * mm});
            skArc(sketch, "E638", {"start": v(-45.36, -13.29) * mm, "mid": v(-45.42, -13.33) * mm, "end": v(-45.48, -13.37) * mm});
            skArc(sketch, "E639", {"start": v(-45.48, -13.37) * mm, "mid": v(-45.54, -13.44) * mm, "end": v(-45.56, -13.53) * mm});
            skArc(sketch, "E640", {"start": v(-46.09, -11.6) * mm, "mid": v(-46.03, -11.82) * mm, "end": v(-45.98, -12.03) * mm});
            skArc(sketch, "E641", {"start": v(-46.44, -10.1) * mm, "mid": v(-46.38, -10.16) * mm, "end": v(-46.3, -10.2) * mm});
            skArc(sketch, "E642", {"start": v(-46.3, -10.2) * mm, "mid": v(-46.22, -10.2) * mm, "end": v(-46.15, -10.2) * mm});
            skArc(sketch, "E643", {"start": v(-45.87, -11.38) * mm, "mid": v(-45.54, -10.68) * mm, "end": v(-46.15, -10.2) * mm});
            skArc(sketch, "E644", {"start": v(-45.87, -11.38) * mm, "mid": v(-45.94, -11.41) * mm, "end": v(-46, -11.46) * mm});
            skArc(sketch, "E645", {"start": v(-46, -11.46) * mm, "mid": v(-46.06, -11.53) * mm, "end": v(-46.09, -11.6) * mm});
            skArc(sketch, "E646", {"start": v(-46.53, -9.67) * mm, "mid": v(-46.49, -9.88) * mm, "end": v(-46.44, -10.1) * mm});
            skArc(sketch, "E647", {"start": v(-46.82, -8.14) * mm, "mid": v(-46.76, -8.2) * mm, "end": v(-46.68, -8.24) * mm});
            skArc(sketch, "E648", {"start": v(-46.68, -8.24) * mm, "mid": v(-46.6, -8.26) * mm, "end": v(-46.53, -8.27) * mm});
            skArc(sketch, "E649", {"start": v(-46.3, -9.45) * mm, "mid": v(-45.95, -8.76) * mm, "end": v(-46.53, -8.27) * mm});
            skArc(sketch, "E650", {"start": v(-46.3, -9.45) * mm, "mid": v(-46.38, -9.48) * mm, "end": v(-46.44, -9.52) * mm});
            skArc(sketch, "E651", {"start": v(-46.44, -9.52) * mm, "mid": v(-46.5, -9.59) * mm, "end": v(-46.53, -9.67) * mm});
            skArc(sketch, "E652", {"start": v(-46.9, -7.71) * mm, "mid": v(-46.86, -7.93) * mm, "end": v(-46.82, -8.14) * mm});
            skArc(sketch, "E653", {"start": v(-47.12, -6.17) * mm, "mid": v(-47.07, -6.24) * mm, "end": v(-46.99, -6.28) * mm});
            skArc(sketch, "E654", {"start": v(-46.99, -6.28) * mm, "mid": v(-46.91, -6.3) * mm, "end": v(-46.84, -6.3) * mm});
            skArc(sketch, "E655", {"start": v(-46.66, -7.5) * mm, "mid": v(-46.27, -6.83) * mm, "end": v(-46.84, -6.3) * mm});
            skArc(sketch, "E656", {"start": v(-46.66, -7.5) * mm, "mid": v(-46.73, -7.53) * mm, "end": v(-46.8, -7.57) * mm});
            skArc(sketch, "E657", {"start": v(-46.8, -7.57) * mm, "mid": v(-46.86, -7.63) * mm, "end": v(-46.9, -7.71) * mm});
            skArc(sketch, "E658", {"start": v(-47.18, -5.74) * mm, "mid": v(-47.15, -5.96) * mm, "end": v(-47.12, -6.17) * mm});
            skArc(sketch, "E659", {"start": v(-47.34, -4.2) * mm, "mid": v(-47.29, -4.26) * mm, "end": v(-47.21, -4.3) * mm});
            skArc(sketch, "E660", {"start": v(-47.21, -4.3) * mm, "mid": v(-47.14, -4.33) * mm, "end": v(-47.06, -4.34) * mm});
            skArc(sketch, "E661", {"start": v(-46.94, -5.54) * mm, "mid": v(-46.52, -4.89) * mm, "end": v(-47.06, -4.34) * mm});
            skArc(sketch, "E662", {"start": v(-46.94, -5.54) * mm, "mid": v(-47, -5.57) * mm, "end": v(-47.07, -5.6) * mm});
            skArc(sketch, "E663", {"start": v(-47.07, -5.6) * mm, "mid": v(-47.14, -5.66) * mm, "end": v(-47.18, -5.74) * mm});
            skArc(sketch, "E664", {"start": v(-47.38, -3.76) * mm, "mid": v(-47.36, -3.98) * mm, "end": v(-47.34, -4.2) * mm});
            skArc(sketch, "E665", {"start": v(-47.47, -2.2) * mm, "mid": v(-47.42, -2.28) * mm, "end": v(-47.35, -2.33) * mm});
            skArc(sketch, "E666", {"start": v(-47.35, -2.33) * mm, "mid": v(-47.28, -2.35) * mm, "end": v(-47.2, -2.37) * mm});
            skArc(sketch, "E667", {"start": v(-47.13, -3.57) * mm, "mid": v(-46.68, -2.94) * mm, "end": v(-47.2, -2.37) * mm});
            skArc(sketch, "E668", {"start": v(-47.13, -3.57) * mm, "mid": v(-47.2, -3.6) * mm, "end": v(-47.27, -3.63) * mm});
            skArc(sketch, "E669", {"start": v(-47.27, -3.63) * mm, "mid": v(-47.34, -3.68) * mm, "end": v(-47.38, -3.76) * mm});
            skArc(sketch, "E670", {"start": v(-47.5, -1.77) * mm, "mid": v(-47.48, -2) * mm, "end": v(-47.47, -2.2) * mm});
            skArc(sketch, "E671", {"start": v(-47.52, -0.22) * mm, "mid": v(-47.48, -0.3) * mm, "end": v(-47.4, -0.34) * mm});
            skArc(sketch, "E672", {"start": v(-47.4, -0.34) * mm, "mid": v(-47.33, -0.37) * mm, "end": v(-47.26, -0.39) * mm});
            skArc(sketch, "E673", {"start": v(-47.24, -1.59) * mm, "mid": v(-46.77, -0.98) * mm, "end": v(-47.26, -0.39) * mm});
            skArc(sketch, "E674", {"start": v(-47.24, -1.59) * mm, "mid": v(-47.3, -1.61) * mm, "end": v(-47.38, -1.64) * mm});
            skArc(sketch, "E675", {"start": v(-47.38, -1.64) * mm, "mid": v(-47.45, -1.7) * mm, "end": v(-47.5, -1.77) * mm});
            skArc(sketch, "E676", {"start": v(-47.52, 0.22) * mm, "mid": v(-47.52, 0) * mm, "end": v(-47.52, -0.22) * mm});
            skArc(sketch, "E677", {"start": v(-47.5, 1.77) * mm, "mid": v(-47.45, 1.7) * mm, "end": v(-47.38, 1.64) * mm});
            skArc(sketch, "E678", {"start": v(-47.38, 1.64) * mm, "mid": v(-47.3, 1.61) * mm, "end": v(-47.24, 1.59) * mm});
            skArc(sketch, "E679", {"start": v(-47.26, 0.39) * mm, "mid": v(-46.77, 0.98) * mm, "end": v(-47.24, 1.59) * mm});
            skArc(sketch, "E680", {"start": v(-47.26, 0.39) * mm, "mid": v(-47.33, 0.37) * mm, "end": v(-47.4, 0.34) * mm});
            skArc(sketch, "E681", {"start": v(-47.4, 0.34) * mm, "mid": v(-47.48, 0.3) * mm, "end": v(-47.52, 0.22) * mm});
            skArc(sketch, "E682", {"start": v(-47.47, 2.2) * mm, "mid": v(-47.48, 2) * mm, "end": v(-47.5, 1.77) * mm});
            skArc(sketch, "E683", {"start": v(-47.38, 3.76) * mm, "mid": v(-47.34, 3.68) * mm, "end": v(-47.27, 3.63) * mm});
            skArc(sketch, "E684", {"start": v(-47.27, 3.63) * mm, "mid": v(-47.2, 3.6) * mm, "end": v(-47.13, 3.57) * mm});
            skArc(sketch, "E685", {"start": v(-47.2, 2.37) * mm, "mid": v(-46.68, 2.94) * mm, "end": v(-47.13, 3.57) * mm});
            skArc(sketch, "E686", {"start": v(-47.2, 2.37) * mm, "mid": v(-47.28, 2.35) * mm, "end": v(-47.35, 2.33) * mm});
            skArc(sketch, "E687", {"start": v(-47.35, 2.33) * mm, "mid": v(-47.42, 2.28) * mm, "end": v(-47.47, 2.2) * mm});
            skArc(sketch, "E688", {"start": v(-47.34, 4.2) * mm, "mid": v(-47.36, 3.98) * mm, "end": v(-47.38, 3.76) * mm});
            skArc(sketch, "E689", {"start": v(-47.18, 5.74) * mm, "mid": v(-47.14, 5.66) * mm, "end": v(-47.07, 5.6) * mm});
            skArc(sketch, "E690", {"start": v(-47.07, 5.6) * mm, "mid": v(-47, 5.57) * mm, "end": v(-46.94, 5.54) * mm});
            skArc(sketch, "E691", {"start": v(-47.06, 4.34) * mm, "mid": v(-46.52, 4.89) * mm, "end": v(-46.94, 5.54) * mm});
            skArc(sketch, "E692", {"start": v(-47.06, 4.34) * mm, "mid": v(-47.14, 4.33) * mm, "end": v(-47.21, 4.3) * mm});
            skArc(sketch, "E693", {"start": v(-47.21, 4.3) * mm, "mid": v(-47.29, 4.26) * mm, "end": v(-47.34, 4.2) * mm});
            skArc(sketch, "E694", {"start": v(-47.12, 6.17) * mm, "mid": v(-47.15, 5.96) * mm, "end": v(-47.18, 5.74) * mm});
            skArc(sketch, "E695", {"start": v(-46.9, 7.71) * mm, "mid": v(-46.86, 7.63) * mm, "end": v(-46.8, 7.57) * mm});
            skArc(sketch, "E696", {"start": v(-46.8, 7.57) * mm, "mid": v(-46.73, 7.53) * mm, "end": v(-46.66, 7.5) * mm});
            skArc(sketch, "E697", {"start": v(-46.84, 6.3) * mm, "mid": v(-46.27, 6.83) * mm, "end": v(-46.66, 7.5) * mm});
            skArc(sketch, "E698", {"start": v(-46.84, 6.3) * mm, "mid": v(-46.91, 6.3) * mm, "end": v(-46.99, 6.28) * mm});
            skArc(sketch, "E699", {"start": v(-46.99, 6.28) * mm, "mid": v(-47.07, 6.24) * mm, "end": v(-47.12, 6.17) * mm});
            skArc(sketch, "E700", {"start": v(-46.82, 8.14) * mm, "mid": v(-46.86, 7.93) * mm, "end": v(-46.9, 7.71) * mm});
            skArc(sketch, "E701", {"start": v(-46.53, 9.67) * mm, "mid": v(-46.5, 9.59) * mm, "end": v(-46.44, 9.52) * mm});
            skArc(sketch, "E702", {"start": v(-46.44, 9.52) * mm, "mid": v(-46.38, 9.48) * mm, "end": v(-46.3, 9.45) * mm});
            skArc(sketch, "E703", {"start": v(-46.53, 8.27) * mm, "mid": v(-45.95, 8.76) * mm, "end": v(-46.3, 9.45) * mm});
            skArc(sketch, "E704", {"start": v(-46.53, 8.27) * mm, "mid": v(-46.6, 8.26) * mm, "end": v(-46.68, 8.24) * mm});
            skArc(sketch, "E705", {"start": v(-46.68, 8.24) * mm, "mid": v(-46.76, 8.2) * mm, "end": v(-46.82, 8.14) * mm});
            skArc(sketch, "E706", {"start": v(-46.44, 10.1) * mm, "mid": v(-46.49, 9.88) * mm, "end": v(-46.53, 9.67) * mm});
            skArc(sketch, "E707", {"start": v(-46.09, 11.6) * mm, "mid": v(-46.06, 11.53) * mm, "end": v(-46, 11.46) * mm});
            skArc(sketch, "E708", {"start": v(-46, 11.46) * mm, "mid": v(-45.94, 11.41) * mm, "end": v(-45.87, 11.38) * mm});
            skArc(sketch, "E709", {"start": v(-46.15, 10.2) * mm, "mid": v(-45.54, 10.68) * mm, "end": v(-45.87, 11.38) * mm});
            skArc(sketch, "E710", {"start": v(-46.15, 10.2) * mm, "mid": v(-46.22, 10.2) * mm, "end": v(-46.3, 10.2) * mm});
            skArc(sketch, "E711", {"start": v(-46.3, 10.2) * mm, "mid": v(-46.38, 10.16) * mm, "end": v(-46.44, 10.1) * mm});
            skArc(sketch, "E712", {"start": v(-45.98, 12.03) * mm, "mid": v(-46.03, 11.82) * mm, "end": v(-46.09, 11.6) * mm});
            skArc(sketch, "E713", {"start": v(-45.56, 13.53) * mm, "mid": v(-45.54, 13.44) * mm, "end": v(-45.48, 13.37) * mm});
            skArc(sketch, "E714", {"start": v(-45.48, 13.37) * mm, "mid": v(-45.42, 13.33) * mm, "end": v(-45.36, 13.29) * mm});
            skArc(sketch, "E715", {"start": v(-45.68, 12.13) * mm, "mid": v(-45.05, 12.58) * mm, "end": v(-45.36, 13.29) * mm});
            skArc(sketch, "E716", {"start": v(-45.68, 12.13) * mm, "mid": v(-45.76, 12.13) * mm, "end": v(-45.83, 12.12) * mm});
            skArc(sketch, "E717", {"start": v(-45.83, 12.12) * mm, "mid": v(-45.91, 12.09) * mm, "end": v(-45.98, 12.03) * mm});
            skArc(sketch, "E718", {"start": v(-45.43, 13.94) * mm, "mid": v(-45.5, 13.74) * mm, "end": v(-45.56, 13.53) * mm});
            skArc(sketch, "E719", {"start": v(-44.95, 15.43) * mm, "mid": v(-44.93, 15.34) * mm, "end": v(-44.88, 15.27) * mm});
            skArc(sketch, "E720", {"start": v(-44.88, 15.27) * mm, "mid": v(-44.82, 15.22) * mm, "end": v(-44.76, 15.17) * mm});
            skArc(sketch, "E721", {"start": v(-45.13, 14.03) * mm, "mid": v(-44.49, 14.45) * mm, "end": v(-44.76, 15.17) * mm});
            skArc(sketch, "E722", {"start": v(-45.13, 14.03) * mm, "mid": v(-45.2, 14.04) * mm, "end": v(-45.28, 14.03) * mm});
            skArc(sketch, "E723", {"start": v(-45.28, 14.03) * mm, "mid": v(-45.37, 14) * mm, "end": v(-45.43, 13.94) * mm});
            skArc(sketch, "E724", {"start": v(-44.8, 15.83) * mm, "mid": v(-44.88, 15.63) * mm, "end": v(-44.95, 15.43) * mm});
            skArc(sketch, "E725", {"start": v(-44.27, 17.3) * mm, "mid": v(-44.25, 17.2) * mm, "end": v(-44.2, 17.13) * mm});
            skArc(sketch, "E726", {"start": v(-44.2, 17.13) * mm, "mid": v(-44.15, 17.08) * mm, "end": v(-44.09, 17.04) * mm});
            skArc(sketch, "E727", {"start": v(-44.5, 15.91) * mm, "mid": v(-43.84, 16.3) * mm, "end": v(-44.09, 17.04) * mm});
            skArc(sketch, "E728", {"start": v(-44.5, 15.91) * mm, "mid": v(-44.58, 15.92) * mm, "end": v(-44.66, 15.91) * mm});
            skArc(sketch, "E729", {"start": v(-44.66, 15.91) * mm, "mid": v(-44.74, 15.89) * mm, "end": v(-44.8, 15.83) * mm});
            skArc(sketch, "E730", {"start": v(-44.1, 17.7) * mm, "mid": v(-44.19, 17.5) * mm, "end": v(-44.27, 17.3) * mm});
            skArc(sketch, "E731", {"start": v(-43.5, 19.13) * mm, "mid": v(-43.5, 19.04) * mm, "end": v(-43.45, 18.97) * mm});
            skArc(sketch, "E732", {"start": v(-43.45, 18.97) * mm, "mid": v(-43.4, 18.91) * mm, "end": v(-43.33, 18.87) * mm});
            skArc(sketch, "E733", {"start": v(-43.8, 17.76) * mm, "mid": v(-43.12, 18.13) * mm, "end": v(-43.33, 18.87) * mm});
            skArc(sketch, "E734", {"start": v(-43.8, 17.76) * mm, "mid": v(-43.87, 17.77) * mm, "end": v(-43.95, 17.77) * mm});
            skArc(sketch, "E735", {"start": v(-43.95, 17.77) * mm, "mid": v(-44.04, 17.75) * mm, "end": v(-44.1, 17.7) * mm});
            skArc(sketch, "E736", {"start": v(-43.33, 19.53) * mm, "mid": v(-43.42, 19.33) * mm, "end": v(-43.5, 19.13) * mm});
            skArc(sketch, "E737", {"start": v(-42.66, 20.94) * mm, "mid": v(-42.66, 20.85) * mm, "end": v(-42.61, 20.77) * mm});
            skArc(sketch, "E738", {"start": v(-42.61, 20.77) * mm, "mid": v(-42.56, 20.71) * mm, "end": v(-42.5, 20.66) * mm});
            skArc(sketch, "E739", {"start": v(-43.02, 19.58) * mm, "mid": v(-42.32, 19.92) * mm, "end": v(-42.5, 20.66) * mm});
            skArc(sketch, "E740", {"start": v(-43.02, 19.58) * mm, "mid": v(-43.1, 19.6) * mm, "end": v(-43.17, 19.6) * mm});
            skArc(sketch, "E741", {"start": v(-43.17, 19.6) * mm, "mid": v(-43.25, 19.58) * mm, "end": v(-43.33, 19.53) * mm});
            skArc(sketch, "E742", {"start": v(-42.47, 21.32) * mm, "mid": v(-42.57, 21.13) * mm, "end": v(-42.66, 20.94) * mm});
            skArc(sketch, "E743", {"start": v(-41.75, 22.7) * mm, "mid": v(-41.74, 22.62) * mm, "end": v(-41.7, 22.54) * mm});
            skArc(sketch, "E744", {"start": v(-41.7, 22.54) * mm, "mid": v(-41.66, 22.48) * mm, "end": v(-41.6, 22.43) * mm});
            skArc(sketch, "E745", {"start": v(-42.16, 21.36) * mm, "mid": v(-41.45, 21.67) * mm, "end": v(-41.6, 22.43) * mm});
            skArc(sketch, "E746", {"start": v(-42.16, 21.36) * mm, "mid": v(-42.23, 21.38) * mm, "end": v(-42.3, 21.38) * mm});
            skArc(sketch, "E747", {"start": v(-42.3, 21.38) * mm, "mid": v(-42.4, 21.37) * mm, "end": v(-42.47, 21.32) * mm});
            skArc(sketch, "E748", {"start": v(-41.54, 23.08) * mm, "mid": v(-41.65, 22.9) * mm, "end": v(-41.75, 22.7) * mm});
            skArc(sketch, "E749", {"start": v(-40.76, 24.43) * mm, "mid": v(-40.76, 24.35) * mm, "end": v(-40.73, 24.26) * mm});
            skArc(sketch, "E750", {"start": v(-40.73, 24.26) * mm, "mid": v(-40.68, 24.2) * mm, "end": v(-40.63, 24.15) * mm});
            skArc(sketch, "E751", {"start": v(-41.23, 23.1) * mm, "mid": v(-40.5, 23.39) * mm, "end": v(-40.63, 24.15) * mm});
            skArc(sketch, "E752", {"start": v(-41.23, 23.1) * mm, "mid": v(-41.3, 23.13) * mm, "end": v(-41.38, 23.14) * mm});
            skArc(sketch, "E753", {"start": v(-41.38, 23.14) * mm, "mid": v(-41.46, 23.13) * mm, "end": v(-41.54, 23.08) * mm});
            skArc(sketch, "E754", {"start": v(-40.54, 24.8) * mm, "mid": v(-40.65, 24.62) * mm, "end": v(-40.76, 24.43) * mm});
            skArc(sketch, "E755", {"start": v(-39.7, 26.12) * mm, "mid": v(-39.7, 26.03) * mm, "end": v(-39.67, 25.95) * mm});
            skArc(sketch, "E756", {"start": v(-39.67, 25.95) * mm, "mid": v(-39.63, 25.89) * mm, "end": v(-39.58, 25.83) * mm});
            skArc(sketch, "E757", {"start": v(-40.22, 24.82) * mm, "mid": v(-39.5, 25.06) * mm, "end": v(-39.58, 25.83) * mm});
            skArc(sketch, "E758", {"start": v(-40.22, 24.82) * mm, "mid": v(-40.3, 24.84) * mm, "end": v(-40.37, 24.85) * mm});
            skArc(sketch, "E759", {"start": v(-40.37, 24.85) * mm, "mid": v(-40.46, 24.84) * mm, "end": v(-40.54, 24.8) * mm});
            skArc(sketch, "E760", {"start": v(-39.46, 26.48) * mm, "mid": v(-39.58, 26.3) * mm, "end": v(-39.7, 26.12) * mm});
            skArc(sketch, "E761", {"start": v(-38.58, 27.76) * mm, "mid": v(-38.58, 27.67) * mm, "end": v(-38.55, 27.59) * mm});
            skArc(sketch, "E762", {"start": v(-38.55, 27.59) * mm, "mid": v(-38.51, 27.52) * mm, "end": v(-38.46, 27.46) * mm});
            skArc(sketch, "E763", {"start": v(-39.15, 26.48) * mm, "mid": v(-38.4, 26.7) * mm, "end": v(-38.46, 27.46) * mm});
            skArc(sketch, "E764", {"start": v(-39.15, 26.48) * mm, "mid": v(-39.22, 26.5) * mm, "end": v(-39.3, 26.52) * mm});
            skArc(sketch, "E765", {"start": v(-39.3, 26.52) * mm, "mid": v(-39.38, 26.52) * mm, "end": v(-39.46, 26.48) * mm});
            skArc(sketch, "E766", {"start": v(-38.32, 28.1) * mm, "mid": v(-38.45, 27.93) * mm, "end": v(-38.58, 27.76) * mm});
            skArc(sketch, "E767", {"start": v(-37.38, 29.35) * mm, "mid": v(-37.39, 29.26) * mm, "end": v(-37.36, 29.18) * mm});
            skArc(sketch, "E768", {"start": v(-37.36, 29.18) * mm, "mid": v(-37.33, 29.11) * mm, "end": v(-37.28, 29.05) * mm});
            skArc(sketch, "E769", {"start": v(-38, 28.1) * mm, "mid": v(-37.26, 28.28) * mm, "end": v(-37.28, 29.05) * mm});
            skArc(sketch, "E770", {"start": v(-38, 28.1) * mm, "mid": v(-38.08, 28.12) * mm, "end": v(-38.15, 28.14) * mm});
            skArc(sketch, "E771", {"start": v(-38.15, 28.14) * mm, "mid": v(-38.24, 28.14) * mm, "end": v(-38.32, 28.1) * mm});
            skArc(sketch, "E772", {"start": v(-37.11, 29.69) * mm, "mid": v(-37.25, 29.52) * mm, "end": v(-37.38, 29.35) * mm});
            skArc(sketch, "E773", {"start": v(-36.12, 30.89) * mm, "mid": v(-36.13, 30.8) * mm, "end": v(-36.1, 30.72) * mm});
            skArc(sketch, "E774", {"start": v(-36.1, 30.72) * mm, "mid": v(-36.07, 30.65) * mm, "end": v(-36.03, 30.59) * mm});
            skArc(sketch, "E775", {"start": v(-36.8, 29.66) * mm, "mid": v(-36.04, 29.82) * mm, "end": v(-36.03, 30.59) * mm});
            skArc(sketch, "E776", {"start": v(-36.8, 29.66) * mm, "mid": v(-36.87, 29.7) * mm, "end": v(-36.94, 29.71) * mm});
            skArc(sketch, "E777", {"start": v(-36.94, 29.71) * mm, "mid": v(-37.03, 29.72) * mm, "end": v(-37.11, 29.69) * mm});
            skArc(sketch, "E778", {"start": v(-35.83, 31.22) * mm, "mid": v(-35.98, 31.05) * mm, "end": v(-36.12, 30.89) * mm});
            skArc(sketch, "E779", {"start": v(-34.8, 32.38) * mm, "mid": v(-34.8, 32.29) * mm, "end": v(-34.8, 32.2) * mm});
            skArc(sketch, "E780", {"start": v(-34.8, 32.2) * mm, "mid": v(-34.76, 32.13) * mm, "end": v(-34.72, 32.07) * mm});
            skArc(sketch, "E781", {"start": v(-35.52, 31.18) * mm, "mid": v(-34.76, 31.3) * mm, "end": v(-34.72, 32.07) * mm});
            skArc(sketch, "E782", {"start": v(-35.52, 31.18) * mm, "mid": v(-35.59, 31.2) * mm, "end": v(-35.66, 31.24) * mm});
            skArc(sketch, "E783", {"start": v(-35.66, 31.24) * mm, "mid": v(-35.75, 31.24) * mm, "end": v(-35.83, 31.22) * mm});
            skArc(sketch, "E784", {"start": v(-34.5, 32.7) * mm, "mid": v(-34.64, 32.53) * mm, "end": v(-34.8, 32.38) * mm});
            skArc(sketch, "E785", {"start": v(-33.4, 33.8) * mm, "mid": v(-33.43, 33.72) * mm, "end": v(-33.41, 33.63) * mm});
            skArc(sketch, "E786", {"start": v(-33.41, 33.63) * mm, "mid": v(-33.38, 33.56) * mm, "end": v(-33.34, 33.5) * mm});
            skArc(sketch, "E787", {"start": v(-34.18, 32.64) * mm, "mid": v(-33.42, 32.73) * mm, "end": v(-33.34, 33.5) * mm});
            skArc(sketch, "E788", {"start": v(-34.18, 32.64) * mm, "mid": v(-34.25, 32.67) * mm, "end": v(-34.32, 32.7) * mm});
            skArc(sketch, "E789", {"start": v(-34.32, 32.7) * mm, "mid": v(-34.41, 32.71) * mm, "end": v(-34.5, 32.7) * mm});
            skArc(sketch, "E790", {"start": v(-33.1, 34.1) * mm, "mid": v(-33.25, 33.96) * mm, "end": v(-33.4, 33.8) * mm});
            skArc(sketch, "E791", {"start": v(-31.96, 35.17) * mm, "mid": v(-31.98, 35.09) * mm, "end": v(-31.98, 35) * mm});
            skArc(sketch, "E792", {"start": v(-31.98, 35) * mm, "mid": v(-31.95, 34.93) * mm, "end": v(-31.91, 34.86) * mm});
            skArc(sketch, "E793", {"start": v(-32.79, 34.04) * mm, "mid": v(-32.02, 34.1) * mm, "end": v(-31.91, 34.86) * mm});
            skArc(sketch, "E794", {"start": v(-32.79, 34.04) * mm, "mid": v(-32.85, 34.08) * mm, "end": v(-32.92, 34.1) * mm});
            skArc(sketch, "E795", {"start": v(-32.92, 34.1) * mm, "mid": v(-33.01, 34.12) * mm, "end": v(-33.1, 34.1) * mm});
            skArc(sketch, "E796", {"start": v(-31.64, 35.46) * mm, "mid": v(-31.8, 35.32) * mm, "end": v(-31.96, 35.17) * mm});
            skArc(sketch, "E797", {"start": v(-30.46, 36.48) * mm, "mid": v(-30.49, 36.4) * mm, "end": v(-30.48, 36.3) * mm});
            skArc(sketch, "E798", {"start": v(-30.48, 36.3) * mm, "mid": v(-30.46, 36.24) * mm, "end": v(-30.43, 36.17) * mm});
            skArc(sketch, "E799", {"start": v(-31.33, 35.38) * mm, "mid": v(-30.56, 35.4) * mm, "end": v(-30.43, 36.17) * mm});
            skArc(sketch, "E800", {"start": v(-31.33, 35.38) * mm, "mid": v(-31.4, 35.42) * mm, "end": v(-31.47, 35.46) * mm});
            skArc(sketch, "E801", {"start": v(-31.47, 35.46) * mm, "mid": v(-31.55, 35.48) * mm, "end": v(-31.64, 35.46) * mm});
            skArc(sketch, "E802", {"start": v(-30.13, 36.76) * mm, "mid": v(-30.3, 36.62) * mm, "end": v(-30.46, 36.48) * mm});
            skArc(sketch, "E803", {"start": v(-28.9, 37.72) * mm, "mid": v(-28.94, 37.64) * mm, "end": v(-28.93, 37.55) * mm});
            skArc(sketch, "E804", {"start": v(-28.93, 37.55) * mm, "mid": v(-28.91, 37.48) * mm, "end": v(-28.88, 37.4) * mm});
            skArc(sketch, "E805", {"start": v(-29.82, 36.66) * mm, "mid": v(-29.05, 36.66) * mm, "end": v(-28.88, 37.4) * mm});
            skArc(sketch, "E806", {"start": v(-29.82, 36.66) * mm, "mid": v(-29.89, 36.7) * mm, "end": v(-29.95, 36.74) * mm});
            skArc(sketch, "E807", {"start": v(-29.95, 36.74) * mm, "mid": v(-30.04, 36.77) * mm, "end": v(-30.13, 36.76) * mm});
            skArc(sketch, "E808", {"start": v(-28.56, 37.99) * mm, "mid": v(-28.73, 37.86) * mm, "end": v(-28.9, 37.72) * mm});
            skArc(sketch, "E809", {"start": v(-27.3, 38.9) * mm, "mid": v(-27.33, 38.82) * mm, "end": v(-27.34, 38.73) * mm});
            skArc(sketch, "E810", {"start": v(-27.34, 38.73) * mm, "mid": v(-27.32, 38.66) * mm, "end": v(-27.3, 38.59) * mm});
            skArc(sketch, "E811", {"start": v(-28.26, 37.88) * mm, "mid": v(-27.5, 37.84) * mm, "end": v(-27.3, 38.59) * mm});
            skArc(sketch, "E812", {"start": v(-28.26, 37.88) * mm, "mid": v(-28.32, 37.93) * mm, "end": v(-28.39, 37.97) * mm});
            skArc(sketch, "E813", {"start": v(-28.39, 37.97) * mm, "mid": v(-28.47, 38) * mm, "end": v(-28.56, 37.99) * mm});
            skArc(sketch, "E814", {"start": v(-26.95, 39.15) * mm, "mid": v(-27.12, 39.03) * mm, "end": v(-27.3, 38.9) * mm});
            skArc(sketch, "E815", {"start": v(-25.65, 40.01) * mm, "mid": v(-25.69, 39.93) * mm, "end": v(-25.7, 39.84) * mm});
            skArc(sketch, "E816", {"start": v(-25.7, 39.84) * mm, "mid": v(-25.68, 39.77) * mm, "end": v(-25.65, 39.7) * mm});
            skArc(sketch, "E817", {"start": v(-26.65, 39.03) * mm, "mid": v(-25.89, 38.96) * mm, "end": v(-25.65, 39.7) * mm});
            skArc(sketch, "E818", {"start": v(-26.65, 39.03) * mm, "mid": v(-26.71, 39.08) * mm, "end": v(-26.77, 39.12) * mm});
            skArc(sketch, "E819", {"start": v(-26.77, 39.12) * mm, "mid": v(-26.86, 39.15) * mm, "end": v(-26.95, 39.15) * mm});
            skArc(sketch, "E820", {"start": v(-25.28, 40.24) * mm, "mid": v(-25.47, 40.13) * mm, "end": v(-25.65, 40.01) * mm});
            skArc(sketch, "E821", {"start": v(-23.95, 41.05) * mm, "mid": v(-24, 40.97) * mm, "end": v(-24, 40.88) * mm});
            skArc(sketch, "E822", {"start": v(-24, 40.88) * mm, "mid": v(-23.99, 40.8) * mm, "end": v(-23.97, 40.73) * mm});
            skArc(sketch, "E823", {"start": v(-25, 40.11) * mm, "mid": v(-24.23, 40.01) * mm, "end": v(-23.97, 40.73) * mm});
            skArc(sketch, "E824", {"start": v(-25, 40.11) * mm, "mid": v(-25.05, 40.16) * mm, "end": v(-25.11, 40.2) * mm});
            skArc(sketch, "E825", {"start": v(-25.11, 40.2) * mm, "mid": v(-25.2, 40.24) * mm, "end": v(-25.28, 40.24) * mm});
            skArc(sketch, "E826", {"start": v(-23.58, 41.27) * mm, "mid": v(-23.76, 41.16) * mm, "end": v(-23.95, 41.05) * mm});
            skArc(sketch, "E827", {"start": v(-22.2, 42.02) * mm, "mid": v(-22.25, 41.94) * mm, "end": v(-22.27, 41.85) * mm});
            skArc(sketch, "E828", {"start": v(-22.27, 41.85) * mm, "mid": v(-22.26, 41.78) * mm, "end": v(-22.24, 41.7) * mm});
            skArc(sketch, "E829", {"start": v(-23.3, 41.12) * mm, "mid": v(-22.53, 40.99) * mm, "end": v(-22.24, 41.7) * mm});
            skArc(sketch, "E830", {"start": v(-23.3, 41.12) * mm, "mid": v(-23.35, 41.18) * mm, "end": v(-23.4, 41.23) * mm});
            skArc(sketch, "E831", {"start": v(-23.4, 41.23) * mm, "mid": v(-23.49, 41.26) * mm, "end": v(-23.58, 41.27) * mm});
            skArc(sketch, "E832", {"start": v(-21.83, 42.22) * mm, "mid": v(-22.02, 42.12) * mm, "end": v(-22.2, 42.02) * mm});
            skArc(sketch, "E833", {"start": v(-20.43, 42.9) * mm, "mid": v(-20.48, 42.83) * mm, "end": v(-20.5, 42.75) * mm});
            skArc(sketch, "E834", {"start": v(-20.5, 42.75) * mm, "mid": v(-20.49, 42.67) * mm, "end": v(-20.47, 42.6) * mm});
            skArc(sketch, "E835", {"start": v(-21.55, 42.06) * mm, "mid": v(-20.8, 41.9) * mm, "end": v(-20.47, 42.6) * mm});
            skArc(sketch, "E836", {"start": v(-21.55, 42.06) * mm, "mid": v(-21.6, 42.12) * mm, "end": v(-21.66, 42.17) * mm});
            skArc(sketch, "E837", {"start": v(-21.66, 42.17) * mm, "mid": v(-21.74, 42.2) * mm, "end": v(-21.83, 42.22) * mm});
            skArc(sketch, "E838", {"start": v(-20.04, 43.1) * mm, "mid": v(-20.24, 43) * mm, "end": v(-20.43, 42.9) * mm});
            skArc(sketch, "E839", {"start": v(-18.62, 43.73) * mm, "mid": v(-18.67, 43.65) * mm, "end": v(-18.69, 43.57) * mm});
            skArc(sketch, "E840", {"start": v(-18.69, 43.57) * mm, "mid": v(-18.68, 43.5) * mm, "end": v(-18.67, 43.42) * mm});
            skArc(sketch, "E841", {"start": v(-19.77, 42.93) * mm, "mid": v(-19.03, 42.73) * mm, "end": v(-18.67, 43.42) * mm});
            skArc(sketch, "E842", {"start": v(-19.77, 42.93) * mm, "mid": v(-19.82, 42.99) * mm, "end": v(-19.87, 43.04) * mm});
            skArc(sketch, "E843", {"start": v(-19.87, 43.04) * mm, "mid": v(-19.95, 43.08) * mm, "end": v(-20.04, 43.1) * mm});
            skArc(sketch, "E844", {"start": v(-18.22, 43.9) * mm, "mid": v(-18.42, 43.81) * mm, "end": v(-18.62, 43.73) * mm});
            skArc(sketch, "E845", {"start": v(-16.77, 44.47) * mm, "mid": v(-16.82, 44.4) * mm, "end": v(-16.85, 44.31) * mm});
            skArc(sketch, "E846", {"start": v(-16.85, 44.31) * mm, "mid": v(-16.85, 44.24) * mm, "end": v(-16.84, 44.16) * mm});
            skArc(sketch, "E847", {"start": v(-17.96, 43.72) * mm, "mid": v(-17.22, 43.5) * mm, "end": v(-16.84, 44.16) * mm});
            skArc(sketch, "E848", {"start": v(-17.96, 43.72) * mm, "mid": v(-18, 43.78) * mm, "end": v(-18.05, 43.83) * mm});
            skArc(sketch, "E849", {"start": v(-18.05, 43.83) * mm, "mid": v(-18.13, 43.88) * mm, "end": v(-18.22, 43.9) * mm});
            skArc(sketch, "E850", {"start": v(-16.36, 44.62) * mm, "mid": v(-16.57, 44.54) * mm, "end": v(-16.77, 44.47) * mm});
            skArc(sketch, "E851", {"start": v(-14.9, 45.13) * mm, "mid": v(-14.95, 45.06) * mm, "end": v(-14.97, 44.98) * mm});
            skArc(sketch, "E852", {"start": v(-14.97, 44.98) * mm, "mid": v(-14.98, 44.9) * mm, "end": v(-14.97, 44.83) * mm});
            skArc(sketch, "E853", {"start": v(-16.1, 44.43) * mm, "mid": v(-15.38, 44.17) * mm, "end": v(-14.97, 44.83) * mm});
            skArc(sketch, "E854", {"start": v(-16.1, 44.43) * mm, "mid": v(-16.15, 44.5) * mm, "end": v(-16.2, 44.55) * mm});
            skArc(sketch, "E855", {"start": v(-16.2, 44.55) * mm, "mid": v(-16.28, 44.6) * mm, "end": v(-16.36, 44.62) * mm});
            skArc(sketch, "E856", {"start": v(-14.48, 45.27) * mm, "mid": v(-14.69, 45.2) * mm, "end": v(-14.9, 45.13) * mm});
            skArc(sketch, "E857", {"start": v(-12.99, 45.72) * mm, "mid": v(-13.05, 45.65) * mm, "end": v(-13.08, 45.57) * mm});
            skArc(sketch, "E858", {"start": v(-13.08, 45.57) * mm, "mid": v(-13.09, 45.5) * mm, "end": v(-13.08, 45.41) * mm});
            skArc(sketch, "E859", {"start": v(-14.23, 45.07) * mm, "mid": v(-13.52, 44.78) * mm, "end": v(-13.08, 45.41) * mm});
            skArc(sketch, "E860", {"start": v(-14.23, 45.07) * mm, "mid": v(-14.27, 45.13) * mm, "end": v(-14.32, 45.2) * mm});
            skArc(sketch, "E861", {"start": v(-14.32, 45.2) * mm, "mid": v(-14.4, 45.24) * mm, "end": v(-14.48, 45.27) * mm});
            skArc(sketch, "E862", {"start": v(-12.57, 45.83) * mm, "mid": v(-12.78, 45.77) * mm, "end": v(-12.99, 45.72) * mm});
            skArc(sketch, "E863", {"start": v(-11.06, 46.22) * mm, "mid": v(-11.12, 46.16) * mm, "end": v(-11.16, 46.07) * mm});
            skArc(sketch, "E864", {"start": v(-11.16, 46.07) * mm, "mid": v(-11.17, 46) * mm, "end": v(-11.17, 45.92) * mm});
            skArc(sketch, "E865", {"start": v(-12.33, 45.62) * mm, "mid": v(-11.63, 45.3) * mm, "end": v(-11.17, 45.92) * mm});
            skArc(sketch, "E866", {"start": v(-12.33, 45.62) * mm, "mid": v(-12.37, 45.7) * mm, "end": v(-12.42, 45.75) * mm});
            skArc(sketch, "E867", {"start": v(-12.42, 45.75) * mm, "mid": v(-12.49, 45.8) * mm, "end": v(-12.57, 45.83) * mm});
            skArc(sketch, "E868", {"start": v(-10.64, 46.32) * mm, "mid": v(-10.85, 46.27) * mm, "end": v(-11.06, 46.22) * mm});
            skArc(sketch, "E869", {"start": v(-9.12, 46.64) * mm, "mid": v(-9.18, 46.58) * mm, "end": v(-9.22, 46.5) * mm});
            skArc(sketch, "E870", {"start": v(-9.22, 46.5) * mm, "mid": v(-9.23, 46.43) * mm, "end": v(-9.24, 46.35) * mm});
            skArc(sketch, "E871", {"start": v(-10.41, 46.1) * mm, "mid": v(-9.73, 45.75) * mm, "end": v(-9.24, 46.35) * mm});
            skArc(sketch, "E872", {"start": v(-10.41, 46.1) * mm, "mid": v(-10.45, 46.17) * mm, "end": v(-10.5, 46.23) * mm});
            skArc(sketch, "E873", {"start": v(-10.5, 46.23) * mm, "mid": v(-10.56, 46.29) * mm, "end": v(-10.64, 46.32) * mm});
            skArc(sketch, "E874", {"start": v(-8.7, 46.72) * mm, "mid": v(-8.9, 46.68) * mm, "end": v(-9.12, 46.64) * mm});
            skArc(sketch, "E875", {"start": v(-7.16, 46.98) * mm, "mid": v(-7.22, 46.93) * mm, "end": v(-7.26, 46.85) * mm});
            skArc(sketch, "E876", {"start": v(-7.26, 46.85) * mm, "mid": v(-7.28, 46.77) * mm, "end": v(-7.29, 46.7) * mm});
            skArc(sketch, "E877", {"start": v(-8.47, 46.5) * mm, "mid": v(-7.8, 46.12) * mm, "end": v(-7.29, 46.7) * mm});
            skArc(sketch, "E878", {"start": v(-8.47, 46.5) * mm, "mid": v(-8.5, 46.57) * mm, "end": v(-8.55, 46.63) * mm});
            skArc(sketch, "E879", {"start": v(-8.55, 46.63) * mm, "mid": v(-8.61, 46.7) * mm, "end": v(-8.7, 46.72) * mm});
            skArc(sketch, "E880", {"start": v(-6.73, 47.05) * mm, "mid": v(-6.94, 47.02) * mm, "end": v(-7.16, 46.98) * mm});
            skArc(sketch, "E881", {"start": v(-5.18, 47.24) * mm, "mid": v(-5.25, 47.19) * mm, "end": v(-5.3, 47.1) * mm});
            skArc(sketch, "E882", {"start": v(-5.3, 47.1) * mm, "mid": v(-5.32, 47.04) * mm, "end": v(-5.33, 46.96) * mm});
            skArc(sketch, "E883", {"start": v(-6.52, 46.81) * mm, "mid": v(-5.86, 46.4) * mm, "end": v(-5.33, 46.96) * mm});
            skArc(sketch, "E884", {"start": v(-6.52, 46.81) * mm, "mid": v(-6.55, 46.88) * mm, "end": v(-6.59, 46.95) * mm});
            skArc(sketch, "E885", {"start": v(-6.59, 46.95) * mm, "mid": v(-6.65, 47.01) * mm, "end": v(-6.73, 47.05) * mm});
            skArc(sketch, "E886", {"start": v(-4.75, 47.29) * mm, "mid": v(-4.97, 47.26) * mm, "end": v(-5.18, 47.24) * mm});
            skArc(sketch, "E887", {"start": v(-3.2, 47.42) * mm, "mid": v(-3.27, 47.37) * mm, "end": v(-3.32, 47.3) * mm});
            skArc(sketch, "E888", {"start": v(-3.32, 47.3) * mm, "mid": v(-3.34, 47.22) * mm, "end": v(-3.36, 47.14) * mm});
            skArc(sketch, "E889", {"start": v(-4.55, 47.04) * mm, "mid": v(-3.91, 46.61) * mm, "end": v(-3.36, 47.14) * mm});
            skArc(sketch, "E890", {"start": v(-4.55, 47.04) * mm, "mid": v(-4.58, 47.11) * mm, "end": v(-4.61, 47.18) * mm});
            skArc(sketch, "E891", {"start": v(-4.61, 47.18) * mm, "mid": v(-4.67, 47.25) * mm, "end": v(-4.75, 47.29) * mm});
            skArc(sketch, "E892", {"start": v(-2.77, 47.44) * mm, "mid": v(-2.98, 47.43) * mm, "end": v(-3.2, 47.42) * mm});
            skArc(sketch, "E893", {"start": v(-1.21, 47.5) * mm, "mid": v(-1.29, 47.46) * mm, "end": v(-1.34, 47.39) * mm});
            skArc(sketch, "E894", {"start": v(-1.34, 47.39) * mm, "mid": v(-1.36, 47.32) * mm, "end": v(-1.38, 47.24) * mm});
            skArc(sketch, "E895", {"start": v(-2.58, 47.2) * mm, "mid": v(-1.96, 46.73) * mm, "end": v(-1.38, 47.24) * mm});
            skArc(sketch, "E896", {"start": v(-2.58, 47.2) * mm, "mid": v(-2.6, 47.26) * mm, "end": v(-2.63, 47.33) * mm});
            skArc(sketch, "E897", {"start": v(-2.63, 47.33) * mm, "mid": v(-2.7, 47.4) * mm, "end": v(-2.77, 47.44) * mm});
            skArc(sketch, "E898", {"start": v(-0.78, 47.52) * mm, "mid": v(-1, 47.51) * mm, "end": v(-1.21, 47.5) * mm});
            skArc(sketch, "E899", {"start": v(0.78, 47.52) * mm, "mid": v(0.7, 47.47) * mm, "end": v(0.65, 47.4) * mm});
            skArc(sketch, "E900", {"start": v(0.65, 47.4) * mm, "mid": v(0.62, 47.33) * mm, "end": v(0.6, 47.26) * mm});
            skArc(sketch, "E901", {"start": v(-0.6, 47.26) * mm, "mid": v(0, 46.78) * mm, "end": v(0.6, 47.26) * mm});
            skArc(sketch, "E902", {"start": v(-0.6, 47.26) * mm, "mid": v(-0.62, 47.33) * mm, "end": v(-0.65, 47.4) * mm});
            skArc(sketch, "E903", {"start": v(-0.65, 47.4) * mm, "mid": v(-0.7, 47.47) * mm, "end": v(-0.78, 47.52) * mm});
            skArc(sketch, "E904", {"start": v(1.21, 47.5) * mm, "mid": v(1, 47.51) * mm, "end": v(0.78, 47.52) * mm});
            skArc(sketch, "E905", {"start": v(3.2, 47.42) * mm, "mid": v(2.98, 47.43) * mm, "end": v(2.77, 47.44) * mm});
            skArc(sketch, "E906", {"start": v(1.34, 47.39) * mm, "mid": v(1.29, 47.46) * mm, "end": v(1.21, 47.5) * mm});
            skArc(sketch, "E907", {"start": v(1.38, 47.24) * mm, "mid": v(1.36, 47.32) * mm, "end": v(1.34, 47.39) * mm});
            skArc(sketch, "E908", {"start": v(1.38, 47.24) * mm, "mid": v(1.96, 46.73) * mm, "end": v(2.58, 47.2) * mm});
            skArc(sketch, "E909", {"start": v(2.63, 47.33) * mm, "mid": v(2.6, 47.26) * mm, "end": v(2.58, 47.2) * mm});
            skArc(sketch, "E910", {"start": v(2.77, 47.44) * mm, "mid": v(2.7, 47.4) * mm, "end": v(2.63, 47.33) * mm});
            skSolve(sketch);
        }
        {
            var Q0;
            Q0=makeQuery(id+"F0.imprint","IMPRINT",FACE,{"disambiguationData":[TD([[makeQuery(id+"F0.imprint","IMPRINT",EDGE,{"derivedFrom":sQuery(id+"F0.wireOp",EDGE,"E0")}),1.0]])]});
            extrude(context, id + "F1", {"entities" : qUnion([Q0]), "depth" : 25 * mm, "offsetDistance" : 25 * mm});
        }
    });
